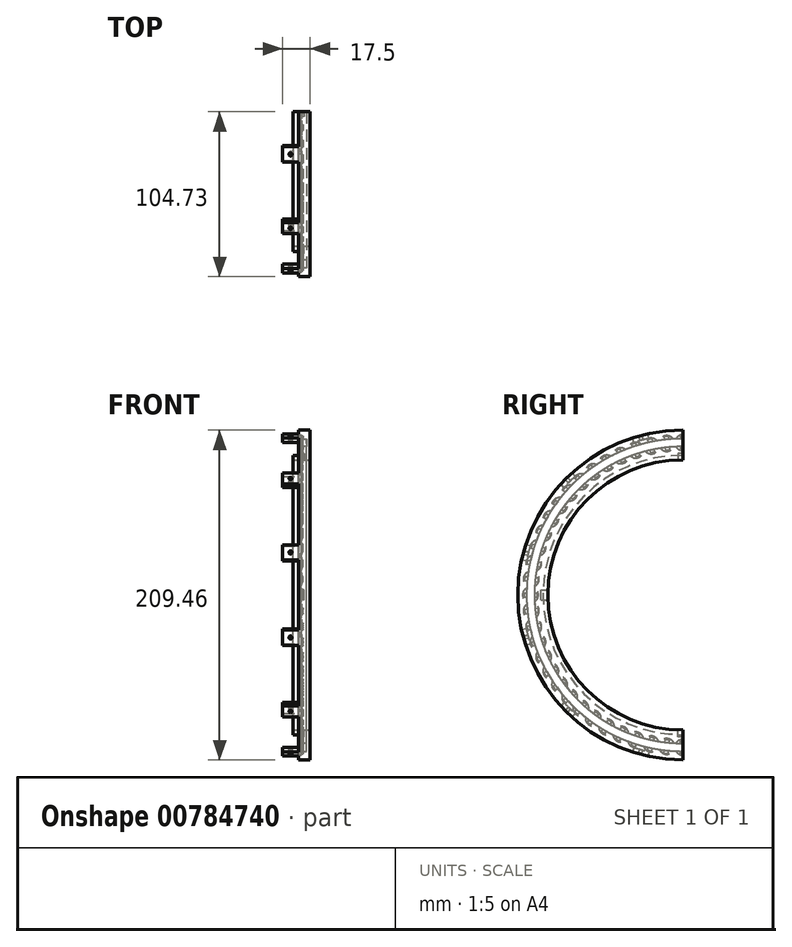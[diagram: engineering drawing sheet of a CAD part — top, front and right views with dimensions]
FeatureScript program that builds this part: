
annotation { "Feature Type Name" : "Feature", "Feature Type Description" : "" }
export const myFeature = defineFeature(function(context is Context, id is Id, definition is map)
    precondition{}
    {
        {
            var Q0;
            Q0=qCreatedBy(makeId("Front.planeOp"),FACE);
            var sketch = newSketch(context, id + "F0", { "sketchPlane" : qUnion([Q0])});
            skLineSegment(sketch, "E0.bottom", {"start": v(-125, 105) * mm, "end": v(125, 105) * mm, "construction": true});
            skLineSegment(sketch, "E0.top", {"start": v(-125, -105) * mm, "end": v(125, -105) * mm, "construction": true});
            skLineSegment(sketch, "E0.left", {"start": v(-125, 105) * mm, "end": v(-125, -105) * mm, "construction": true});
            skLineSegment(sketch, "E0.right", {"start": v(125, 105) * mm, "end": v(125, -105) * mm, "construction": true});
            skLineSegment(sketch, "E1", {"start": v(-16.75, 85.73) * mm, "end": v(-16.75, 88.73) * mm});
            skLineSegment(sketch, "E2", {"start": v(-16.75, 88.73) * mm, "end": v(-13.25, 88.73) * mm});
            skLineSegment(sketch, "E3", {"start": v(-16.75, 85.73) * mm, "end": v(-5.75, 85.73) * mm});
            skLineSegment(sketch, "E4", {"start": v(-5.75, 85.73) * mm, "end": v(-5.75, 104.73) * mm});
            skLineSegment(sketch, "E5", {"start": v(-13.25, 104.73) * mm, "end": v(-13.25, 99.23) * mm});
            skLineSegment(sketch, "E6", {"start": v(-13.25, 99.23) * mm, "end": v(-8.25, 99.23) * mm});
            skLineSegment(sketch, "E7", {"start": v(-8.25, 99.23) * mm, "end": v(-8.25, 94.23) * mm});
            skLineSegment(sketch, "E8", {"start": v(-8.25, 94.23) * mm, "end": v(-13.25, 94.23) * mm});
            skLineSegment(sketch, "E9.trimOffspring", {"start": v(-13.25, 94.23) * mm, "end": v(-13.25, 88.73) * mm});
            skLineSegment(sketch, "E10", {"start": v(-74.95, 0) * mm, "end": v(74.95, 0) * mm});
            skLineSegment(sketch, "E11", {"start": v(-13.25, 104.73) * mm, "end": v(-8.75, 104.73) * mm});
            skLineSegment(sketch, "E12.trimOffspring", {"start": v(-7.75, 104.73) * mm, "end": v(-5.75, 104.73) * mm});
            skLineSegment(sketch, "E13", {"start": v(-7.75, 104.73) * mm, "end": v(-8.75, 104.73) * mm});
            skSolve(sketch);
        }
        {
            var Q0;
            Q0=qSketchRegion(id+"F0",true);
            var Q1;
            Q1=sQuery(id+"F0.wireOp",EDGE,"E10");
            revolve(context, id + "F1", {"surfaceOperationType" : NewSurfaceOperationType.NEW, "entities" : qUnion([Q0]), "axis" : qUnion([Q1]), "revolveType" : RevolveType.ONE_DIRECTION, "angle" : 180 * degree});
        }
        {
            var Q0;
            Q0=qCreatedBy(makeId("Top.planeOp"),FACE);
            cPlane(context, id + "F2", {"entities" : qUnion([Q0]), "cplaneType" : CPlaneType.OFFSET, "offset" : 80 * mm, "oppositeDirection" : true, "width" : 150 * mm, "height" : 150 * mm});
        }
        {
            var Q0;
            Q0=qCreatedBy(id+"F2.planeOp",FACE);
            var sketch = newSketch(context, id + "F3", { "sketchPlane" : qUnion([Q0])});
            skLineSegment(sketch, "E14.top", {"start": v(-9.65, -3.1) * mm, "end": v(-12.85, -3.1) * mm});
            skLineSegment(sketch, "E14.left", {"start": v(-9.65, 0) * mm, "end": v(-9.65, -3.1) * mm});
            skLineSegment(sketch, "E14.right", {"start": v(-12.85, 0) * mm, "end": v(-12.85, -3.1) * mm});
            skLineSegment(sketch, "E15.top", {"start": v(-9.65, 1.57) * mm, "end": v(-12.85, 1.57) * mm});
            skLineSegment(sketch, "E15.left", {"start": v(-9.65, 0) * mm, "end": v(-9.65, 1.57) * mm});
            skLineSegment(sketch, "E15.right", {"start": v(-12.85, 0) * mm, "end": v(-12.85, 1.57) * mm});
            skSolve(sketch);
        }
        {
            var Q0;
            Q0=qSketchRegion(id+"F3",true);
            var Q1;
            Q1=makeQuery(id+"F1.opRevolve","SWEPT_FACE",FACE,{"disambiguationData":[OSD([sQuery(id+"F0.wireOp",EDGE,"E2")])]});
            extrude(context, id + "F4", {"entities" : qUnion([Q0]), "operationType" : NewBodyOperationType.REMOVE, "oppositeDirection" : true, "depth" : 10 * mm, "endBoundEntityFace" : qUnion([Q1]), "offsetDistance" : 25 * mm});
        }
        {
            var Q0;
            Q0=qCreatedBy(makeId("Front.planeOp"),FACE);
            cPlane(context, id + "F5", {"entities" : qUnion([Q0]), "cplaneType" : CPlaneType.OFFSET, "offset" : 80 * mm, "width" : 150 * mm, "height" : 150 * mm});
        }
        {
            var Q0;
            Q0=qCreatedBy(makeId("Top.planeOp"),FACE);
            cPlane(context, id + "F6", {"entities" : qUnion([Q0]), "cplaneType" : CPlaneType.OFFSET, "offset" : 80 * mm, "width" : 150 * mm, "height" : 150 * mm});
        }
        {
            var Q0;
            Q0=qCreatedBy(id+"F5.planeOp",FACE);
            var sketch = newSketch(context, id + "F7", { "sketchPlane" : qUnion([Q0])});
            skLineSegment(sketch, "E16.bottom", {"start": v(-9.65, -3.1) * mm, "end": v(-12.85, -3.1) * mm});
            skLineSegment(sketch, "E16.top", {"start": v(-9.65, 3.1) * mm, "end": v(-12.85, 3.1) * mm});
            skLineSegment(sketch, "E16.left", {"start": v(-9.65, -3.1) * mm, "end": v(-9.65, 3.1) * mm});
            skLineSegment(sketch, "E16.right", {"start": v(-12.85, -3.1) * mm, "end": v(-12.85, 3.1) * mm});
            skSolve(sketch);
        }
        {
            var Q0;
            Q0=qSketchRegion(id+"F7",true);
            var Q1;
            Q1=makeQuery(id+"F1.opRevolve","SWEPT_FACE",FACE,{"disambiguationData":[OSD([sQuery(id+"F0.wireOp",EDGE,"E2")])]});
            extrude(context, id + "F8", {"entities" : qUnion([Q0]), "operationType" : NewBodyOperationType.REMOVE, "depth" : 10 * mm, "endBoundEntityFace" : qUnion([Q1]), "offsetDistance" : 25 * mm});
        }
        {
            var Q0;
            Q0=qCreatedBy(id+"F6.planeOp",FACE);
            var sketch = newSketch(context, id + "F9", { "sketchPlane" : qUnion([Q0])});
            skLineSegment(sketch, "E17.bottom", {"start": v(-9.65, 0) * mm, "end": v(-12.85, 0) * mm});
            skLineSegment(sketch, "E17.top", {"start": v(-9.65, -3.1) * mm, "end": v(-12.85, -3.1) * mm});
            skLineSegment(sketch, "E17.left", {"start": v(-9.65, 0) * mm, "end": v(-9.65, -3.1) * mm});
            skLineSegment(sketch, "E17.right", {"start": v(-12.85, 0) * mm, "end": v(-12.85, -3.1) * mm});
            skSolve(sketch);
        }
        {
            var Q0;
            Q0=qSketchRegion(id+"F9",true);
            var Q1;
            Q1=makeQuery(id+"F1.opRevolve","SWEPT_FACE",FACE,{"disambiguationData":[OSD([sQuery(id+"F0.wireOp",EDGE,"E2")])]});
            extrude(context, id + "F10", {"entities" : qUnion([Q0]), "operationType" : NewBodyOperationType.REMOVE, "depth" : 10 * mm, "endBoundEntityFace" : qUnion([Q1]), "offsetDistance" : 25 * mm});
        }
        {
            var Q0;
            Q0=makeQuery(id+"F1.opRevolve","SWEPT_FACE",FACE,{"disambiguationData":[OSD([sQuery(id+"F0.wireOp",EDGE,"E7")])]});
            var sketch = newSketch(context, id + "F11", { "sketchPlane" : qUnion([Q0])});
            skCircle(sketch, "E18", {"center": v(0, 96.73) * mm, "radius": 5 * mm});
            skCircle(sketch, "E19.1.0", {"center": v(-10.11, 96.2) * mm, "radius": 5 * mm});
            skCircle(sketch, "E19.2.0", {"center": v(-20.11, 94.62) * mm, "radius": 5 * mm});
            skCircle(sketch, "E19.3.0", {"center": v(-29.9, 92) * mm, "radius": 5 * mm});
            skCircle(sketch, "E19.4.0", {"center": v(-39.34, 88.37) * mm, "radius": 5 * mm});
            skCircle(sketch, "E19.5.0", {"center": v(-48.36, 83.77) * mm, "radius": 5 * mm});
            skCircle(sketch, "E19.6.0", {"center": v(-56.86, 78.26) * mm, "radius": 5 * mm});
            skCircle(sketch, "E19.7.0", {"center": v(-64.73, 71.88) * mm, "radius": 5 * mm});
            skCircle(sketch, "E19.8.0", {"center": v(-71.88, 64.73) * mm, "radius": 5 * mm});
            skCircle(sketch, "E19.9.0", {"center": v(-78.26, 56.86) * mm, "radius": 5 * mm});
            skCircle(sketch, "E19.10.0", {"center": v(-83.77, 48.36) * mm, "radius": 5 * mm});
            skCircle(sketch, "E19.11.0", {"center": v(-88.37, 39.34) * mm, "radius": 5 * mm});
            skCircle(sketch, "E19.12.0", {"center": v(-92, 29.9) * mm, "radius": 5 * mm});
            skCircle(sketch, "E19.13.0", {"center": v(-94.62, 20.11) * mm, "radius": 5 * mm});
            skCircle(sketch, "E19.14.0", {"center": v(-96.2, 10.11) * mm, "radius": 5 * mm});
            skCircle(sketch, "E19.15.0", {"center": v(-96.73, 0) * mm, "radius": 5 * mm});
            skCircle(sketch, "E19.16.0", {"center": v(-96.2, -10.11) * mm, "radius": 5 * mm});
            skCircle(sketch, "E19.17.0", {"center": v(-94.62, -20.11) * mm, "radius": 5 * mm});
            skCircle(sketch, "E19.18.0", {"center": v(-92, -29.9) * mm, "radius": 5 * mm});
            skCircle(sketch, "E19.19.0", {"center": v(-88.37, -39.34) * mm, "radius": 5 * mm});
            skCircle(sketch, "E19.20.0", {"center": v(-83.77, -48.36) * mm, "radius": 5 * mm});
            skCircle(sketch, "E19.21.0", {"center": v(-78.26, -56.86) * mm, "radius": 5 * mm});
            skCircle(sketch, "E19.22.0", {"center": v(-71.88, -64.73) * mm, "radius": 5 * mm});
            skCircle(sketch, "E19.23.0", {"center": v(-64.73, -71.88) * mm, "radius": 5 * mm});
            skCircle(sketch, "E19.24.0", {"center": v(-56.86, -78.26) * mm, "radius": 5 * mm});
            skCircle(sketch, "E19.25.0", {"center": v(-48.36, -83.77) * mm, "radius": 5 * mm});
            skCircle(sketch, "E19.26.0", {"center": v(-39.34, -88.37) * mm, "radius": 5 * mm});
            skCircle(sketch, "E19.27.0", {"center": v(-29.9, -92) * mm, "radius": 5 * mm});
            skCircle(sketch, "E19.28.0", {"center": v(-20.11, -94.62) * mm, "radius": 5 * mm});
            skCircle(sketch, "E19.29.0", {"center": v(-10.11, -96.2) * mm, "radius": 5 * mm});
            skCircle(sketch, "E19.30.0", {"center": v(0, -96.73) * mm, "radius": 5 * mm});
            skCircle(sketch, "E19.31.0", {"center": v(10.11, -96.2) * mm, "radius": 5 * mm});
            skCircle(sketch, "E19.32.0", {"center": v(20.11, -94.62) * mm, "radius": 5 * mm});
            skCircle(sketch, "E19.33.0", {"center": v(29.9, -92) * mm, "radius": 5 * mm});
            skCircle(sketch, "E19.34.0", {"center": v(39.34, -88.37) * mm, "radius": 5 * mm});
            skCircle(sketch, "E19.35.0", {"center": v(48.36, -83.77) * mm, "radius": 5 * mm});
            skCircle(sketch, "E19.36.0", {"center": v(56.86, -78.26) * mm, "radius": 5 * mm});
            skCircle(sketch, "E19.37.0", {"center": v(64.73, -71.88) * mm, "radius": 5 * mm});
            skCircle(sketch, "E19.38.0", {"center": v(71.88, -64.73) * mm, "radius": 5 * mm});
            skCircle(sketch, "E19.39.0", {"center": v(78.26, -56.86) * mm, "radius": 5 * mm});
            skCircle(sketch, "E19.40.0", {"center": v(83.77, -48.37) * mm, "radius": 5 * mm});
            skCircle(sketch, "E19.41.0", {"center": v(88.37, -39.34) * mm, "radius": 5 * mm});
            skCircle(sketch, "E19.42.0", {"center": v(92, -29.9) * mm, "radius": 5 * mm});
            skCircle(sketch, "E19.43.0", {"center": v(94.62, -20.11) * mm, "radius": 5 * mm});
            skCircle(sketch, "E19.44.0", {"center": v(96.2, -10.11) * mm, "radius": 5 * mm});
            skCircle(sketch, "E19.45.0", {"center": v(96.73, 0) * mm, "radius": 5 * mm});
            skCircle(sketch, "E19.46.0", {"center": v(96.2, 10.11) * mm, "radius": 5 * mm});
            skCircle(sketch, "E19.47.0", {"center": v(94.62, 20.11) * mm, "radius": 5 * mm});
            skCircle(sketch, "E19.48.0", {"center": v(92, 29.9) * mm, "radius": 5 * mm});
            skCircle(sketch, "E19.49.0", {"center": v(88.37, 39.34) * mm, "radius": 5 * mm});
            skCircle(sketch, "E19.50.0", {"center": v(83.77, 48.36) * mm, "radius": 5 * mm});
            skCircle(sketch, "E19.51.0", {"center": v(78.26, 56.86) * mm, "radius": 5 * mm});
            skCircle(sketch, "E19.52.0", {"center": v(71.88, 64.73) * mm, "radius": 5 * mm});
            skCircle(sketch, "E19.53.0", {"center": v(64.73, 71.88) * mm, "radius": 5 * mm});
            skCircle(sketch, "E19.54.0", {"center": v(56.86, 78.26) * mm, "radius": 5 * mm});
            skCircle(sketch, "E19.55.0", {"center": v(48.36, 83.77) * mm, "radius": 5 * mm});
            skCircle(sketch, "E19.56.0", {"center": v(39.34, 88.37) * mm, "radius": 5 * mm});
            skCircle(sketch, "E19.57.0", {"center": v(29.9, 92) * mm, "radius": 5 * mm});
            skCircle(sketch, "E19.58.0", {"center": v(20.11, 94.62) * mm, "radius": 5 * mm});
            skCircle(sketch, "E19.59.0", {"center": v(10.11, 96.2) * mm, "radius": 5 * mm});
            skPoint(sketch, "E19.center", {"position": v(0, 0) * mm});
            skSolve(sketch);
        }
        {
            var Q0;
            Q0=qSketchRegion(id+"F11",true);
            extrude(context, id + "F12", {"entities" : qUnion([Q0]), "operationType" : NewBodyOperationType.REMOVE, "depth" : 25 * mm, "offsetDistance" : 25 * mm, "hasSecondDirection" : true, "secondDirectionOppositeDirection" : false, "secondDirectionDepth" : 3 * mm});
        }
        {
            var Q0;
            Q0=makeQuery(id+"F1.opRevolve","SWEPT_FACE",FACE,{"disambiguationData":[OSD([sQuery(id+"F0.wireOp",EDGE,"E7")])]});
            var sketch = newSketch(context, id + "F13", { "sketchPlane" : qUnion([Q0])});
            skLineSegment(sketch, "E20.bottom", {"start": v(1.36, 92.48) * mm, "end": v(0, 92.48) * mm});
            skLineSegment(sketch, "E20.top", {"start": v(1.36, 100.98) * mm, "end": v(0, 100.98) * mm});
            skLineSegment(sketch, "E20.left", {"start": v(1.36, 92.48) * mm, "end": v(1.36, 100.98) * mm});
            skLineSegment(sketch, "E21", {"start": v(1.96, 96.73) * mm, "end": v(-1.46, 96.73) * mm, "construction": true});
            skLineSegment(sketch, "E22.MirrorCS", {"start": v(-1.36, 92.48) * mm, "end": v(0, 92.48) * mm});
            skLineSegment(sketch, "E23.MirrorCS", {"start": v(-1.36, 92.48) * mm, "end": v(-1.36, 100.98) * mm});
            skLineSegment(sketch, "E24.MirrorCS", {"start": v(-1.36, 100.98) * mm, "end": v(0, 100.98) * mm});
            skLineSegment(sketch, "E25", {"start": v(0, 92.48) * mm, "end": v(0, 100.98) * mm, "construction": true});
            skLineSegment(sketch, "E26.1.0", {"start": v(-8.32, 92.12) * mm, "end": v(-9.67, 91.97) * mm});
            skLineSegment(sketch, "E26.1.1", {"start": v(-9.2, 100.57) * mm, "end": v(-10.56, 100.43) * mm});
            skLineSegment(sketch, "E26.1.2", {"start": v(-8.32, 92.12) * mm, "end": v(-9.2, 100.57) * mm});
            skLineSegment(sketch, "E26.1.3", {"start": v(-8.16, 96.4) * mm, "end": v(-11.56, 96.05) * mm, "construction": true});
            skLineSegment(sketch, "E26.1.4", {"start": v(-11.02, 91.83) * mm, "end": v(-9.67, 91.97) * mm});
            skLineSegment(sketch, "E26.1.5", {"start": v(-11.02, 91.83) * mm, "end": v(-11.9, 100.28) * mm});
            skLineSegment(sketch, "E26.1.6", {"start": v(-11.9, 100.28) * mm, "end": v(-10.56, 100.43) * mm});
            skLineSegment(sketch, "E26.1.7", {"start": v(-9.67, 91.97) * mm, "end": v(-10.56, 100.43) * mm, "construction": true});
            skLineSegment(sketch, "E26.2.0", {"start": v(-17.9, 90.74) * mm, "end": v(-19.23, 90.46) * mm});
            skLineSegment(sketch, "E26.2.1", {"start": v(-19.67, 99.06) * mm, "end": v(-21, 98.77) * mm});
            skLineSegment(sketch, "E26.2.2", {"start": v(-17.9, 90.74) * mm, "end": v(-19.67, 99.06) * mm});
            skLineSegment(sketch, "E26.2.3", {"start": v(-18.2, 95.02) * mm, "end": v(-21.54, 94.31) * mm, "construction": true});
            skLineSegment(sketch, "E26.2.4", {"start": v(-20.56, 90.18) * mm, "end": v(-19.23, 90.46) * mm});
            skLineSegment(sketch, "E26.2.5", {"start": v(-20.56, 90.18) * mm, "end": v(-22.32, 98.5) * mm});
            skLineSegment(sketch, "E26.2.6", {"start": v(-22.32, 98.5) * mm, "end": v(-21, 98.77) * mm});
            skLineSegment(sketch, "E26.2.7", {"start": v(-19.23, 90.46) * mm, "end": v(-21, 98.77) * mm, "construction": true});
            skLineSegment(sketch, "E26.3.0", {"start": v(-27.29, 88.37) * mm, "end": v(-28.58, 87.95) * mm});
            skLineSegment(sketch, "E26.3.1", {"start": v(-29.91, 96.46) * mm, "end": v(-31.2, 96.04) * mm});
            skLineSegment(sketch, "E26.3.2", {"start": v(-27.29, 88.37) * mm, "end": v(-29.91, 96.46) * mm});
            skLineSegment(sketch, "E26.3.3", {"start": v(-28.02, 92.6) * mm, "end": v(-31.28, 91.54) * mm, "construction": true});
            skLineSegment(sketch, "E26.3.4", {"start": v(-29.87, 87.53) * mm, "end": v(-28.58, 87.95) * mm});
            skLineSegment(sketch, "E26.3.5", {"start": v(-29.87, 87.53) * mm, "end": v(-32.5, 95.62) * mm});
            skLineSegment(sketch, "E26.3.6", {"start": v(-32.5, 95.62) * mm, "end": v(-31.2, 96.04) * mm});
            skLineSegment(sketch, "E26.3.7", {"start": v(-28.58, 87.95) * mm, "end": v(-31.2, 96.04) * mm, "construction": true});
            skLineSegment(sketch, "E26.4.0", {"start": v(-36.37, 85.04) * mm, "end": v(-37.62, 84.48) * mm});
            skLineSegment(sketch, "E26.4.1", {"start": v(-39.83, 92.8) * mm, "end": v(-41.07, 92.25) * mm});
            skLineSegment(sketch, "E26.4.2", {"start": v(-36.37, 85.04) * mm, "end": v(-39.83, 92.8) * mm});
            skLineSegment(sketch, "E26.4.3", {"start": v(-37.55, 89.17) * mm, "end": v(-40.68, 87.77) * mm, "construction": true});
            skLineSegment(sketch, "E26.4.4", {"start": v(-38.86, 83.93) * mm, "end": v(-37.62, 84.48) * mm});
            skLineSegment(sketch, "E26.4.5", {"start": v(-38.86, 83.93) * mm, "end": v(-42.31, 91.7) * mm});
            skLineSegment(sketch, "E26.4.6", {"start": v(-42.31, 91.7) * mm, "end": v(-41.07, 92.25) * mm});
            skLineSegment(sketch, "E26.4.7", {"start": v(-37.62, 84.48) * mm, "end": v(-41.07, 92.25) * mm, "construction": true});
            skLineSegment(sketch, "E26.5.0", {"start": v(-45.06, 80.77) * mm, "end": v(-46.24, 80.1) * mm});
            skLineSegment(sketch, "E26.5.1", {"start": v(-49.31, 88.13) * mm, "end": v(-50.49, 87.45) * mm});
            skLineSegment(sketch, "E26.5.2", {"start": v(-45.06, 80.77) * mm, "end": v(-49.31, 88.13) * mm});
            skLineSegment(sketch, "E26.5.3", {"start": v(-46.67, 84.75) * mm, "end": v(-49.63, 83.04) * mm, "construction": true});
            skLineSegment(sketch, "E26.5.4", {"start": v(-47.42, 79.41) * mm, "end": v(-46.24, 80.1) * mm});
            skLineSegment(sketch, "E26.5.5", {"start": v(-47.42, 79.41) * mm, "end": v(-51.67, 86.77) * mm});
            skLineSegment(sketch, "E26.5.6", {"start": v(-51.67, 86.77) * mm, "end": v(-50.49, 87.45) * mm});
            skLineSegment(sketch, "E26.5.7", {"start": v(-46.24, 80.1) * mm, "end": v(-50.49, 87.45) * mm, "construction": true});
            skLineSegment(sketch, "E26.6.0", {"start": v(-53.26, 75.62) * mm, "end": v(-54.36, 74.82) * mm});
            skLineSegment(sketch, "E26.6.1", {"start": v(-58.26, 82.5) * mm, "end": v(-59.35, 81.7) * mm});
            skLineSegment(sketch, "E26.6.2", {"start": v(-53.26, 75.62) * mm, "end": v(-58.26, 82.5) * mm});
            skLineSegment(sketch, "E26.6.3", {"start": v(-55.27, 79.4) * mm, "end": v(-58.04, 77.4) * mm, "construction": true});
            skLineSegment(sketch, "E26.6.4", {"start": v(-55.46, 74.02) * mm, "end": v(-54.36, 74.82) * mm});
            skLineSegment(sketch, "E26.6.5", {"start": v(-55.46, 74.02) * mm, "end": v(-60.45, 80.9) * mm});
            skLineSegment(sketch, "E26.6.6", {"start": v(-60.45, 80.9) * mm, "end": v(-59.35, 81.7) * mm});
            skLineSegment(sketch, "E26.6.7", {"start": v(-54.36, 74.82) * mm, "end": v(-59.35, 81.7) * mm, "construction": true});
            skLineSegment(sketch, "E26.7.0", {"start": v(-60.87, 69.63) * mm, "end": v(-61.88, 68.73) * mm});
            skLineSegment(sketch, "E26.7.1", {"start": v(-66.56, 75.95) * mm, "end": v(-67.57, 75.04) * mm});
            skLineSegment(sketch, "E26.7.2", {"start": v(-60.87, 69.63) * mm, "end": v(-66.56, 75.95) * mm});
            skLineSegment(sketch, "E26.7.3", {"start": v(-63.27, 73.2) * mm, "end": v(-65.8, 70.9) * mm, "construction": true});
            skLineSegment(sketch, "E26.7.4", {"start": v(-62.9, 67.82) * mm, "end": v(-61.88, 68.73) * mm});
            skLineSegment(sketch, "E26.7.5", {"start": v(-62.9, 67.82) * mm, "end": v(-68.58, 74.13) * mm});
            skLineSegment(sketch, "E26.7.6", {"start": v(-68.58, 74.13) * mm, "end": v(-67.57, 75.04) * mm});
            skLineSegment(sketch, "E26.7.7", {"start": v(-61.88, 68.73) * mm, "end": v(-67.57, 75.04) * mm, "construction": true});
            skLineSegment(sketch, "E26.8.0", {"start": v(-67.82, 62.9) * mm, "end": v(-68.73, 61.88) * mm});
            skLineSegment(sketch, "E26.8.1", {"start": v(-74.13, 68.58) * mm, "end": v(-75.04, 67.57) * mm});
            skLineSegment(sketch, "E26.8.2", {"start": v(-67.82, 62.9) * mm, "end": v(-74.13, 68.58) * mm});
            skLineSegment(sketch, "E26.8.3", {"start": v(-70.57, 66.18) * mm, "end": v(-72.86, 63.64) * mm, "construction": true});
            skLineSegment(sketch, "E26.8.4", {"start": v(-69.63, 60.87) * mm, "end": v(-68.73, 61.88) * mm});
            skLineSegment(sketch, "E26.8.5", {"start": v(-69.63, 60.87) * mm, "end": v(-75.95, 66.56) * mm});
            skLineSegment(sketch, "E26.8.6", {"start": v(-75.95, 66.56) * mm, "end": v(-75.04, 67.57) * mm});
            skLineSegment(sketch, "E26.8.7", {"start": v(-68.73, 61.88) * mm, "end": v(-75.04, 67.57) * mm, "construction": true});
            skLineSegment(sketch, "E26.9.0", {"start": v(-74.02, 55.46) * mm, "end": v(-74.82, 54.36) * mm});
            skLineSegment(sketch, "E26.9.1", {"start": v(-80.9, 60.45) * mm, "end": v(-81.7, 59.35) * mm});
            skLineSegment(sketch, "E26.9.2", {"start": v(-74.02, 55.46) * mm, "end": v(-80.9, 60.45) * mm});
            skLineSegment(sketch, "E26.9.3", {"start": v(-77.1, 58.44) * mm, "end": v(-79.11, 55.68) * mm, "construction": true});
            skLineSegment(sketch, "E26.9.4", {"start": v(-75.62, 53.26) * mm, "end": v(-74.82, 54.36) * mm});
            skLineSegment(sketch, "E26.9.5", {"start": v(-75.62, 53.26) * mm, "end": v(-82.5, 58.26) * mm});
            skLineSegment(sketch, "E26.9.6", {"start": v(-82.5, 58.26) * mm, "end": v(-81.7, 59.35) * mm});
            skLineSegment(sketch, "E26.9.7", {"start": v(-74.82, 54.36) * mm, "end": v(-81.7, 59.35) * mm, "construction": true});
            skLineSegment(sketch, "E26.10.0", {"start": v(-79.41, 47.42) * mm, "end": v(-80.1, 46.24) * mm});
            skLineSegment(sketch, "E26.10.1", {"start": v(-86.77, 51.67) * mm, "end": v(-87.45, 50.49) * mm});
            skLineSegment(sketch, "E26.10.2", {"start": v(-79.41, 47.42) * mm, "end": v(-86.77, 51.67) * mm});
            skLineSegment(sketch, "E26.10.3", {"start": v(-82.79, 50.06) * mm, "end": v(-84.5, 47.1) * mm, "construction": true});
            skLineSegment(sketch, "E26.10.4", {"start": v(-80.77, 45.06) * mm, "end": v(-80.1, 46.24) * mm});
            skLineSegment(sketch, "E26.10.5", {"start": v(-80.77, 45.06) * mm, "end": v(-88.13, 49.31) * mm});
            skLineSegment(sketch, "E26.10.6", {"start": v(-88.13, 49.31) * mm, "end": v(-87.45, 50.49) * mm});
            skLineSegment(sketch, "E26.10.7", {"start": v(-80.1, 46.24) * mm, "end": v(-87.45, 50.49) * mm, "construction": true});
            skLineSegment(sketch, "E26.11.0", {"start": v(-83.93, 38.86) * mm, "end": v(-84.48, 37.62) * mm});
            skLineSegment(sketch, "E26.11.1", {"start": v(-91.7, 42.31) * mm, "end": v(-92.25, 41.07) * mm});
            skLineSegment(sketch, "E26.11.2", {"start": v(-83.93, 38.86) * mm, "end": v(-91.7, 42.31) * mm});
            skLineSegment(sketch, "E26.11.3", {"start": v(-87.57, 41.14) * mm, "end": v(-88.96, 38) * mm, "construction": true});
            skLineSegment(sketch, "E26.11.4", {"start": v(-85.04, 36.37) * mm, "end": v(-84.48, 37.62) * mm});
            skLineSegment(sketch, "E26.11.5", {"start": v(-85.04, 36.37) * mm, "end": v(-92.8, 39.83) * mm});
            skLineSegment(sketch, "E26.11.6", {"start": v(-92.8, 39.83) * mm, "end": v(-92.25, 41.07) * mm});
            skLineSegment(sketch, "E26.11.7", {"start": v(-84.48, 37.62) * mm, "end": v(-92.25, 41.07) * mm, "construction": true});
            skLineSegment(sketch, "E26.12.0", {"start": v(-87.53, 29.87) * mm, "end": v(-87.95, 28.58) * mm});
            skLineSegment(sketch, "E26.12.1", {"start": v(-95.62, 32.5) * mm, "end": v(-96.04, 31.2) * mm});
            skLineSegment(sketch, "E26.12.2", {"start": v(-87.53, 29.87) * mm, "end": v(-95.62, 32.5) * mm});
            skLineSegment(sketch, "E26.12.3", {"start": v(-91.39, 31.76) * mm, "end": v(-92.45, 28.5) * mm, "construction": true});
            skLineSegment(sketch, "E26.12.4", {"start": v(-88.37, 27.29) * mm, "end": v(-87.95, 28.58) * mm});
            skLineSegment(sketch, "E26.12.5", {"start": v(-88.37, 27.29) * mm, "end": v(-96.46, 29.91) * mm});
            skLineSegment(sketch, "E26.12.6", {"start": v(-96.46, 29.91) * mm, "end": v(-96.04, 31.2) * mm});
            skLineSegment(sketch, "E26.12.7", {"start": v(-87.95, 28.58) * mm, "end": v(-96.04, 31.2) * mm, "construction": true});
            skLineSegment(sketch, "E26.13.0", {"start": v(-90.18, 20.56) * mm, "end": v(-90.46, 19.23) * mm});
            skLineSegment(sketch, "E26.13.1", {"start": v(-98.5, 22.32) * mm, "end": v(-98.77, 21) * mm});
            skLineSegment(sketch, "E26.13.2", {"start": v(-90.18, 20.56) * mm, "end": v(-98.5, 22.32) * mm});
            skLineSegment(sketch, "E26.13.3", {"start": v(-94.2, 22.03) * mm, "end": v(-94.92, 18.68) * mm, "construction": true});
            skLineSegment(sketch, "E26.13.4", {"start": v(-90.74, 17.9) * mm, "end": v(-90.46, 19.23) * mm});
            skLineSegment(sketch, "E26.13.5", {"start": v(-90.74, 17.9) * mm, "end": v(-99.06, 19.67) * mm});
            skLineSegment(sketch, "E26.13.6", {"start": v(-99.06, 19.67) * mm, "end": v(-98.77, 21) * mm});
            skLineSegment(sketch, "E26.13.7", {"start": v(-90.46, 19.23) * mm, "end": v(-98.77, 21) * mm, "construction": true});
            skLineSegment(sketch, "E26.14.0", {"start": v(-91.83, 11.02) * mm, "end": v(-91.97, 9.67) * mm});
            skLineSegment(sketch, "E26.14.1", {"start": v(-100.28, 11.9) * mm, "end": v(-100.43, 10.56) * mm});
            skLineSegment(sketch, "E26.14.2", {"start": v(-91.83, 11.02) * mm, "end": v(-100.28, 11.9) * mm});
            skLineSegment(sketch, "E26.14.3", {"start": v(-96, 12.06) * mm, "end": v(-96.35, 8.66) * mm, "construction": true});
            skLineSegment(sketch, "E26.14.4", {"start": v(-92.12, 8.32) * mm, "end": v(-91.97, 9.67) * mm});
            skLineSegment(sketch, "E26.14.5", {"start": v(-92.12, 8.32) * mm, "end": v(-100.57, 9.2) * mm});
            skLineSegment(sketch, "E26.14.6", {"start": v(-100.57, 9.2) * mm, "end": v(-100.43, 10.56) * mm});
            skLineSegment(sketch, "E26.14.7", {"start": v(-91.97, 9.67) * mm, "end": v(-100.43, 10.56) * mm, "construction": true});
            skLineSegment(sketch, "E26.15.0", {"start": v(-92.48, 1.36) * mm, "end": v(-92.48, 0) * mm});
            skLineSegment(sketch, "E26.15.1", {"start": v(-100.98, 1.36) * mm, "end": v(-100.98, 0) * mm});
            skLineSegment(sketch, "E26.15.2", {"start": v(-92.48, 1.36) * mm, "end": v(-100.98, 1.36) * mm});
            skLineSegment(sketch, "E26.15.3", {"start": v(-96.73, 1.96) * mm, "end": v(-96.73, -1.46) * mm, "construction": true});
            skLineSegment(sketch, "E26.15.4", {"start": v(-92.48, -1.36) * mm, "end": v(-92.48, 0) * mm});
            skLineSegment(sketch, "E26.15.5", {"start": v(-92.48, -1.36) * mm, "end": v(-100.98, -1.36) * mm});
            skLineSegment(sketch, "E26.15.6", {"start": v(-100.98, -1.36) * mm, "end": v(-100.98, 0) * mm});
            skLineSegment(sketch, "E26.15.7", {"start": v(-92.48, 0) * mm, "end": v(-100.98, 0) * mm, "construction": true});
            skLineSegment(sketch, "E26.16.0", {"start": v(-92.12, -8.32) * mm, "end": v(-91.97, -9.67) * mm});
            skLineSegment(sketch, "E26.16.1", {"start": v(-100.57, -9.2) * mm, "end": v(-100.43, -10.56) * mm});
            skLineSegment(sketch, "E26.16.2", {"start": v(-92.12, -8.32) * mm, "end": v(-100.57, -9.2) * mm});
            skLineSegment(sketch, "E26.16.3", {"start": v(-96.4, -8.16) * mm, "end": v(-96.05, -11.56) * mm, "construction": true});
            skLineSegment(sketch, "E26.16.4", {"start": v(-91.83, -11.02) * mm, "end": v(-91.97, -9.67) * mm});
            skLineSegment(sketch, "E26.16.5", {"start": v(-91.83, -11.02) * mm, "end": v(-100.28, -11.9) * mm});
            skLineSegment(sketch, "E26.16.6", {"start": v(-100.28, -11.9) * mm, "end": v(-100.43, -10.56) * mm});
            skLineSegment(sketch, "E26.16.7", {"start": v(-91.97, -9.67) * mm, "end": v(-100.43, -10.56) * mm, "construction": true});
            skLineSegment(sketch, "E26.17.0", {"start": v(-90.74, -17.9) * mm, "end": v(-90.46, -19.23) * mm});
            skLineSegment(sketch, "E26.17.1", {"start": v(-99.06, -19.67) * mm, "end": v(-98.77, -21) * mm});
            skLineSegment(sketch, "E26.17.2", {"start": v(-90.74, -17.9) * mm, "end": v(-99.06, -19.67) * mm});
            skLineSegment(sketch, "E26.17.3", {"start": v(-95.02, -18.2) * mm, "end": v(-94.31, -21.54) * mm, "construction": true});
            skLineSegment(sketch, "E26.17.4", {"start": v(-90.18, -20.56) * mm, "end": v(-90.46, -19.23) * mm});
            skLineSegment(sketch, "E26.17.5", {"start": v(-90.18, -20.56) * mm, "end": v(-98.5, -22.32) * mm});
            skLineSegment(sketch, "E26.17.6", {"start": v(-98.5, -22.32) * mm, "end": v(-98.77, -21) * mm});
            skLineSegment(sketch, "E26.17.7", {"start": v(-90.46, -19.23) * mm, "end": v(-98.77, -21) * mm, "construction": true});
            skLineSegment(sketch, "E26.18.0", {"start": v(-88.37, -27.29) * mm, "end": v(-87.95, -28.58) * mm});
            skLineSegment(sketch, "E26.18.1", {"start": v(-96.46, -29.91) * mm, "end": v(-96.04, -31.2) * mm});
            skLineSegment(sketch, "E26.18.2", {"start": v(-88.37, -27.29) * mm, "end": v(-96.46, -29.91) * mm});
            skLineSegment(sketch, "E26.18.3", {"start": v(-92.6, -28.02) * mm, "end": v(-91.54, -31.28) * mm, "construction": true});
            skLineSegment(sketch, "E26.18.4", {"start": v(-87.53, -29.87) * mm, "end": v(-87.95, -28.58) * mm});
            skLineSegment(sketch, "E26.18.5", {"start": v(-87.53, -29.87) * mm, "end": v(-95.62, -32.5) * mm});
            skLineSegment(sketch, "E26.18.6", {"start": v(-95.62, -32.5) * mm, "end": v(-96.04, -31.2) * mm});
            skLineSegment(sketch, "E26.18.7", {"start": v(-87.95, -28.58) * mm, "end": v(-96.04, -31.2) * mm, "construction": true});
            skLineSegment(sketch, "E26.19.0", {"start": v(-85.04, -36.37) * mm, "end": v(-84.48, -37.62) * mm});
            skLineSegment(sketch, "E26.19.1", {"start": v(-92.8, -39.83) * mm, "end": v(-92.25, -41.07) * mm});
            skLineSegment(sketch, "E26.19.2", {"start": v(-85.04, -36.37) * mm, "end": v(-92.8, -39.83) * mm});
            skLineSegment(sketch, "E26.19.3", {"start": v(-89.17, -37.55) * mm, "end": v(-87.77, -40.68) * mm, "construction": true});
            skLineSegment(sketch, "E26.19.4", {"start": v(-83.93, -38.86) * mm, "end": v(-84.48, -37.62) * mm});
            skLineSegment(sketch, "E26.19.5", {"start": v(-83.93, -38.86) * mm, "end": v(-91.7, -42.31) * mm});
            skLineSegment(sketch, "E26.19.6", {"start": v(-91.7, -42.31) * mm, "end": v(-92.25, -41.07) * mm});
            skLineSegment(sketch, "E26.19.7", {"start": v(-84.48, -37.62) * mm, "end": v(-92.25, -41.07) * mm, "construction": true});
            skLineSegment(sketch, "E26.20.0", {"start": v(-80.77, -45.06) * mm, "end": v(-80.1, -46.24) * mm});
            skLineSegment(sketch, "E26.20.1", {"start": v(-88.13, -49.31) * mm, "end": v(-87.45, -50.49) * mm});
            skLineSegment(sketch, "E26.20.2", {"start": v(-80.77, -45.06) * mm, "end": v(-88.13, -49.31) * mm});
            skLineSegment(sketch, "E26.20.3", {"start": v(-84.75, -46.67) * mm, "end": v(-83.04, -49.63) * mm, "construction": true});
            skLineSegment(sketch, "E26.20.4", {"start": v(-79.41, -47.42) * mm, "end": v(-80.1, -46.24) * mm});
            skLineSegment(sketch, "E26.20.5", {"start": v(-79.41, -47.42) * mm, "end": v(-86.77, -51.67) * mm});
            skLineSegment(sketch, "E26.20.6", {"start": v(-86.77, -51.67) * mm, "end": v(-87.45, -50.49) * mm});
            skLineSegment(sketch, "E26.20.7", {"start": v(-80.1, -46.24) * mm, "end": v(-87.45, -50.49) * mm, "construction": true});
            skLineSegment(sketch, "E26.21.0", {"start": v(-75.62, -53.26) * mm, "end": v(-74.82, -54.36) * mm});
            skLineSegment(sketch, "E26.21.1", {"start": v(-82.5, -58.26) * mm, "end": v(-81.7, -59.35) * mm});
            skLineSegment(sketch, "E26.21.2", {"start": v(-75.62, -53.26) * mm, "end": v(-82.5, -58.26) * mm});
            skLineSegment(sketch, "E26.21.3", {"start": v(-79.4, -55.27) * mm, "end": v(-77.4, -58.04) * mm, "construction": true});
            skLineSegment(sketch, "E26.21.4", {"start": v(-74.02, -55.46) * mm, "end": v(-74.82, -54.36) * mm});
            skLineSegment(sketch, "E26.21.5", {"start": v(-74.02, -55.46) * mm, "end": v(-80.9, -60.45) * mm});
            skLineSegment(sketch, "E26.21.6", {"start": v(-80.9, -60.45) * mm, "end": v(-81.7, -59.35) * mm});
            skLineSegment(sketch, "E26.21.7", {"start": v(-74.82, -54.36) * mm, "end": v(-81.7, -59.35) * mm, "construction": true});
            skLineSegment(sketch, "E26.22.0", {"start": v(-69.63, -60.87) * mm, "end": v(-68.73, -61.88) * mm});
            skLineSegment(sketch, "E26.22.1", {"start": v(-75.95, -66.56) * mm, "end": v(-75.04, -67.57) * mm});
            skLineSegment(sketch, "E26.22.2", {"start": v(-69.63, -60.87) * mm, "end": v(-75.95, -66.56) * mm});
            skLineSegment(sketch, "E26.22.3", {"start": v(-73.2, -63.27) * mm, "end": v(-70.9, -65.8) * mm, "construction": true});
            skLineSegment(sketch, "E26.22.4", {"start": v(-67.82, -62.9) * mm, "end": v(-68.73, -61.88) * mm});
            skLineSegment(sketch, "E26.22.5", {"start": v(-67.82, -62.9) * mm, "end": v(-74.13, -68.58) * mm});
            skLineSegment(sketch, "E26.22.6", {"start": v(-74.13, -68.58) * mm, "end": v(-75.04, -67.57) * mm});
            skLineSegment(sketch, "E26.22.7", {"start": v(-68.73, -61.88) * mm, "end": v(-75.04, -67.57) * mm, "construction": true});
            skLineSegment(sketch, "E26.23.0", {"start": v(-62.9, -67.82) * mm, "end": v(-61.88, -68.73) * mm});
            skLineSegment(sketch, "E26.23.1", {"start": v(-68.58, -74.13) * mm, "end": v(-67.57, -75.04) * mm});
            skLineSegment(sketch, "E26.23.2", {"start": v(-62.9, -67.82) * mm, "end": v(-68.58, -74.13) * mm});
            skLineSegment(sketch, "E26.23.3", {"start": v(-66.18, -70.57) * mm, "end": v(-63.64, -72.86) * mm, "construction": true});
            skLineSegment(sketch, "E26.23.4", {"start": v(-60.87, -69.63) * mm, "end": v(-61.88, -68.73) * mm});
            skLineSegment(sketch, "E26.23.5", {"start": v(-60.87, -69.63) * mm, "end": v(-66.56, -75.95) * mm});
            skLineSegment(sketch, "E26.23.6", {"start": v(-66.56, -75.95) * mm, "end": v(-67.57, -75.04) * mm});
            skLineSegment(sketch, "E26.23.7", {"start": v(-61.88, -68.73) * mm, "end": v(-67.57, -75.04) * mm, "construction": true});
            skLineSegment(sketch, "E26.24.0", {"start": v(-55.46, -74.02) * mm, "end": v(-54.36, -74.82) * mm});
            skLineSegment(sketch, "E26.24.1", {"start": v(-60.45, -80.9) * mm, "end": v(-59.35, -81.7) * mm});
            skLineSegment(sketch, "E26.24.2", {"start": v(-55.46, -74.02) * mm, "end": v(-60.45, -80.9) * mm});
            skLineSegment(sketch, "E26.24.3", {"start": v(-58.44, -77.1) * mm, "end": v(-55.68, -79.11) * mm, "construction": true});
            skLineSegment(sketch, "E26.24.4", {"start": v(-53.26, -75.62) * mm, "end": v(-54.36, -74.82) * mm});
            skLineSegment(sketch, "E26.24.5", {"start": v(-53.26, -75.62) * mm, "end": v(-58.26, -82.5) * mm});
            skLineSegment(sketch, "E26.24.6", {"start": v(-58.26, -82.5) * mm, "end": v(-59.35, -81.7) * mm});
            skLineSegment(sketch, "E26.24.7", {"start": v(-54.36, -74.82) * mm, "end": v(-59.35, -81.7) * mm, "construction": true});
            skLineSegment(sketch, "E26.25.0", {"start": v(-47.42, -79.41) * mm, "end": v(-46.24, -80.1) * mm});
            skLineSegment(sketch, "E26.25.1", {"start": v(-51.67, -86.77) * mm, "end": v(-50.49, -87.45) * mm});
            skLineSegment(sketch, "E26.25.2", {"start": v(-47.42, -79.41) * mm, "end": v(-51.67, -86.77) * mm});
            skLineSegment(sketch, "E26.25.3", {"start": v(-50.06, -82.79) * mm, "end": v(-47.1, -84.5) * mm, "construction": true});
            skLineSegment(sketch, "E26.25.4", {"start": v(-45.06, -80.77) * mm, "end": v(-46.24, -80.1) * mm});
            skLineSegment(sketch, "E26.25.5", {"start": v(-45.06, -80.77) * mm, "end": v(-49.31, -88.13) * mm});
            skLineSegment(sketch, "E26.25.6", {"start": v(-49.31, -88.13) * mm, "end": v(-50.49, -87.45) * mm});
            skLineSegment(sketch, "E26.25.7", {"start": v(-46.24, -80.1) * mm, "end": v(-50.49, -87.45) * mm, "construction": true});
            skLineSegment(sketch, "E26.26.0", {"start": v(-38.86, -83.93) * mm, "end": v(-37.62, -84.48) * mm});
            skLineSegment(sketch, "E26.26.1", {"start": v(-42.31, -91.7) * mm, "end": v(-41.07, -92.25) * mm});
            skLineSegment(sketch, "E26.26.2", {"start": v(-38.86, -83.93) * mm, "end": v(-42.31, -91.7) * mm});
            skLineSegment(sketch, "E26.26.3", {"start": v(-41.14, -87.57) * mm, "end": v(-38, -88.96) * mm, "construction": true});
            skLineSegment(sketch, "E26.26.4", {"start": v(-36.37, -85.04) * mm, "end": v(-37.62, -84.48) * mm});
            skLineSegment(sketch, "E26.26.5", {"start": v(-36.37, -85.04) * mm, "end": v(-39.83, -92.8) * mm});
            skLineSegment(sketch, "E26.26.6", {"start": v(-39.83, -92.8) * mm, "end": v(-41.07, -92.25) * mm});
            skLineSegment(sketch, "E26.26.7", {"start": v(-37.62, -84.48) * mm, "end": v(-41.07, -92.25) * mm, "construction": true});
            skLineSegment(sketch, "E26.27.0", {"start": v(-29.87, -87.53) * mm, "end": v(-28.58, -87.95) * mm});
            skLineSegment(sketch, "E26.27.1", {"start": v(-32.5, -95.62) * mm, "end": v(-31.2, -96.04) * mm});
            skLineSegment(sketch, "E26.27.2", {"start": v(-29.87, -87.53) * mm, "end": v(-32.5, -95.62) * mm});
            skLineSegment(sketch, "E26.27.3", {"start": v(-31.76, -91.39) * mm, "end": v(-28.5, -92.45) * mm, "construction": true});
            skLineSegment(sketch, "E26.27.4", {"start": v(-27.29, -88.37) * mm, "end": v(-28.58, -87.95) * mm});
            skLineSegment(sketch, "E26.27.5", {"start": v(-27.29, -88.37) * mm, "end": v(-29.91, -96.46) * mm});
            skLineSegment(sketch, "E26.27.6", {"start": v(-29.91, -96.46) * mm, "end": v(-31.2, -96.04) * mm});
            skLineSegment(sketch, "E26.27.7", {"start": v(-28.58, -87.95) * mm, "end": v(-31.2, -96.04) * mm, "construction": true});
            skLineSegment(sketch, "E26.28.0", {"start": v(-20.56, -90.18) * mm, "end": v(-19.23, -90.46) * mm});
            skLineSegment(sketch, "E26.28.1", {"start": v(-22.32, -98.5) * mm, "end": v(-21, -98.77) * mm});
            skLineSegment(sketch, "E26.28.2", {"start": v(-20.56, -90.18) * mm, "end": v(-22.32, -98.5) * mm});
            skLineSegment(sketch, "E26.28.3", {"start": v(-22.03, -94.2) * mm, "end": v(-18.68, -94.92) * mm, "construction": true});
            skLineSegment(sketch, "E26.28.4", {"start": v(-17.9, -90.74) * mm, "end": v(-19.23, -90.46) * mm});
            skLineSegment(sketch, "E26.28.5", {"start": v(-17.9, -90.74) * mm, "end": v(-19.67, -99.06) * mm});
            skLineSegment(sketch, "E26.28.6", {"start": v(-19.67, -99.06) * mm, "end": v(-21, -98.77) * mm});
            skLineSegment(sketch, "E26.28.7", {"start": v(-19.23, -90.46) * mm, "end": v(-21, -98.77) * mm, "construction": true});
            skLineSegment(sketch, "E26.29.0", {"start": v(-11.02, -91.83) * mm, "end": v(-9.67, -91.97) * mm});
            skLineSegment(sketch, "E26.29.1", {"start": v(-11.9, -100.28) * mm, "end": v(-10.56, -100.43) * mm});
            skLineSegment(sketch, "E26.29.2", {"start": v(-11.02, -91.83) * mm, "end": v(-11.9, -100.28) * mm});
            skLineSegment(sketch, "E26.29.3", {"start": v(-12.06, -96) * mm, "end": v(-8.66, -96.35) * mm, "construction": true});
            skLineSegment(sketch, "E26.29.4", {"start": v(-8.32, -92.12) * mm, "end": v(-9.67, -91.97) * mm});
            skLineSegment(sketch, "E26.29.5", {"start": v(-8.32, -92.12) * mm, "end": v(-9.2, -100.57) * mm});
            skLineSegment(sketch, "E26.29.6", {"start": v(-9.2, -100.57) * mm, "end": v(-10.56, -100.43) * mm});
            skLineSegment(sketch, "E26.29.7", {"start": v(-9.67, -91.97) * mm, "end": v(-10.56, -100.43) * mm, "construction": true});
            skLineSegment(sketch, "E26.30.0", {"start": v(-1.36, -92.48) * mm, "end": v(0, -92.48) * mm});
            skLineSegment(sketch, "E26.30.1", {"start": v(-1.36, -100.98) * mm, "end": v(0, -100.98) * mm});
            skLineSegment(sketch, "E26.30.2", {"start": v(-1.36, -92.48) * mm, "end": v(-1.36, -100.98) * mm});
            skLineSegment(sketch, "E26.30.3", {"start": v(-1.96, -96.73) * mm, "end": v(1.46, -96.73) * mm, "construction": true});
            skLineSegment(sketch, "E26.30.4", {"start": v(1.36, -92.48) * mm, "end": v(0, -92.48) * mm});
            skLineSegment(sketch, "E26.30.5", {"start": v(1.36, -92.48) * mm, "end": v(1.36, -100.98) * mm});
            skLineSegment(sketch, "E26.30.6", {"start": v(1.36, -100.98) * mm, "end": v(0, -100.98) * mm});
            skLineSegment(sketch, "E26.30.7", {"start": v(0, -92.48) * mm, "end": v(0, -100.98) * mm, "construction": true});
            skLineSegment(sketch, "E26.31.0", {"start": v(8.32, -92.12) * mm, "end": v(9.67, -91.97) * mm});
            skLineSegment(sketch, "E26.31.1", {"start": v(9.2, -100.57) * mm, "end": v(10.56, -100.43) * mm});
            skLineSegment(sketch, "E26.31.2", {"start": v(8.32, -92.12) * mm, "end": v(9.2, -100.57) * mm});
            skLineSegment(sketch, "E26.31.3", {"start": v(8.16, -96.4) * mm, "end": v(11.56, -96.05) * mm, "construction": true});
            skLineSegment(sketch, "E26.31.4", {"start": v(11.02, -91.83) * mm, "end": v(9.67, -91.97) * mm});
            skLineSegment(sketch, "E26.31.5", {"start": v(11.02, -91.83) * mm, "end": v(11.9, -100.28) * mm});
            skLineSegment(sketch, "E26.31.6", {"start": v(11.9, -100.28) * mm, "end": v(10.56, -100.43) * mm});
            skLineSegment(sketch, "E26.31.7", {"start": v(9.67, -91.97) * mm, "end": v(10.56, -100.43) * mm, "construction": true});
            skLineSegment(sketch, "E26.32.0", {"start": v(17.9, -90.74) * mm, "end": v(19.23, -90.46) * mm});
            skLineSegment(sketch, "E26.32.1", {"start": v(19.67, -99.06) * mm, "end": v(21, -98.77) * mm});
            skLineSegment(sketch, "E26.32.2", {"start": v(17.9, -90.74) * mm, "end": v(19.67, -99.06) * mm});
            skLineSegment(sketch, "E26.32.3", {"start": v(18.2, -95.02) * mm, "end": v(21.54, -94.31) * mm, "construction": true});
            skLineSegment(sketch, "E26.32.4", {"start": v(20.56, -90.18) * mm, "end": v(19.23, -90.46) * mm});
            skLineSegment(sketch, "E26.32.5", {"start": v(20.56, -90.18) * mm, "end": v(22.32, -98.5) * mm});
            skLineSegment(sketch, "E26.32.6", {"start": v(22.32, -98.5) * mm, "end": v(21, -98.77) * mm});
            skLineSegment(sketch, "E26.32.7", {"start": v(19.23, -90.46) * mm, "end": v(21, -98.77) * mm, "construction": true});
            skLineSegment(sketch, "E26.33.0", {"start": v(27.29, -88.37) * mm, "end": v(28.58, -87.95) * mm});
            skLineSegment(sketch, "E26.33.1", {"start": v(29.91, -96.46) * mm, "end": v(31.2, -96.04) * mm});
            skLineSegment(sketch, "E26.33.2", {"start": v(27.29, -88.37) * mm, "end": v(29.91, -96.46) * mm});
            skLineSegment(sketch, "E26.33.3", {"start": v(28.02, -92.6) * mm, "end": v(31.28, -91.54) * mm, "construction": true});
            skLineSegment(sketch, "E26.33.4", {"start": v(29.87, -87.53) * mm, "end": v(28.58, -87.95) * mm});
            skLineSegment(sketch, "E26.33.5", {"start": v(29.87, -87.53) * mm, "end": v(32.5, -95.62) * mm});
            skLineSegment(sketch, "E26.33.6", {"start": v(32.5, -95.62) * mm, "end": v(31.2, -96.04) * mm});
            skLineSegment(sketch, "E26.33.7", {"start": v(28.58, -87.95) * mm, "end": v(31.2, -96.04) * mm, "construction": true});
            skLineSegment(sketch, "E26.34.0", {"start": v(36.37, -85.04) * mm, "end": v(37.62, -84.48) * mm});
            skLineSegment(sketch, "E26.34.1", {"start": v(39.83, -92.8) * mm, "end": v(41.07, -92.25) * mm});
            skLineSegment(sketch, "E26.34.2", {"start": v(36.37, -85.04) * mm, "end": v(39.83, -92.8) * mm});
            skLineSegment(sketch, "E26.34.3", {"start": v(37.55, -89.17) * mm, "end": v(40.68, -87.77) * mm, "construction": true});
            skLineSegment(sketch, "E26.34.4", {"start": v(38.86, -83.93) * mm, "end": v(37.62, -84.48) * mm});
            skLineSegment(sketch, "E26.34.5", {"start": v(38.86, -83.93) * mm, "end": v(42.31, -91.7) * mm});
            skLineSegment(sketch, "E26.34.6", {"start": v(42.31, -91.7) * mm, "end": v(41.07, -92.25) * mm});
            skLineSegment(sketch, "E26.34.7", {"start": v(37.62, -84.48) * mm, "end": v(41.07, -92.25) * mm, "construction": true});
            skLineSegment(sketch, "E26.35.0", {"start": v(45.06, -80.77) * mm, "end": v(46.24, -80.1) * mm});
            skLineSegment(sketch, "E26.35.1", {"start": v(49.31, -88.13) * mm, "end": v(50.49, -87.45) * mm});
            skLineSegment(sketch, "E26.35.2", {"start": v(45.06, -80.77) * mm, "end": v(49.31, -88.13) * mm});
            skLineSegment(sketch, "E26.35.3", {"start": v(46.67, -84.75) * mm, "end": v(49.63, -83.04) * mm, "construction": true});
            skLineSegment(sketch, "E26.35.4", {"start": v(47.42, -79.41) * mm, "end": v(46.24, -80.1) * mm});
            skLineSegment(sketch, "E26.35.5", {"start": v(47.42, -79.41) * mm, "end": v(51.67, -86.77) * mm});
            skLineSegment(sketch, "E26.35.6", {"start": v(51.67, -86.77) * mm, "end": v(50.49, -87.45) * mm});
            skLineSegment(sketch, "E26.35.7", {"start": v(46.24, -80.1) * mm, "end": v(50.49, -87.45) * mm, "construction": true});
            skLineSegment(sketch, "E26.36.0", {"start": v(53.26, -75.62) * mm, "end": v(54.36, -74.82) * mm});
            skLineSegment(sketch, "E26.36.1", {"start": v(58.26, -82.5) * mm, "end": v(59.35, -81.7) * mm});
            skLineSegment(sketch, "E26.36.2", {"start": v(53.26, -75.62) * mm, "end": v(58.26, -82.5) * mm});
            skLineSegment(sketch, "E26.36.3", {"start": v(55.27, -79.4) * mm, "end": v(58.04, -77.4) * mm, "construction": true});
            skLineSegment(sketch, "E26.36.4", {"start": v(55.46, -74.02) * mm, "end": v(54.36, -74.82) * mm});
            skLineSegment(sketch, "E26.36.5", {"start": v(55.46, -74.02) * mm, "end": v(60.45, -80.9) * mm});
            skLineSegment(sketch, "E26.36.6", {"start": v(60.45, -80.9) * mm, "end": v(59.35, -81.7) * mm});
            skLineSegment(sketch, "E26.36.7", {"start": v(54.36, -74.82) * mm, "end": v(59.35, -81.7) * mm, "construction": true});
            skLineSegment(sketch, "E26.37.0", {"start": v(60.87, -69.63) * mm, "end": v(61.88, -68.73) * mm});
            skLineSegment(sketch, "E26.37.1", {"start": v(66.56, -75.95) * mm, "end": v(67.57, -75.04) * mm});
            skLineSegment(sketch, "E26.37.2", {"start": v(60.87, -69.63) * mm, "end": v(66.56, -75.95) * mm});
            skLineSegment(sketch, "E26.37.3", {"start": v(63.27, -73.2) * mm, "end": v(65.8, -70.9) * mm, "construction": true});
            skLineSegment(sketch, "E26.37.4", {"start": v(62.9, -67.82) * mm, "end": v(61.88, -68.73) * mm});
            skLineSegment(sketch, "E26.37.5", {"start": v(62.9, -67.82) * mm, "end": v(68.58, -74.13) * mm});
            skLineSegment(sketch, "E26.37.6", {"start": v(68.58, -74.13) * mm, "end": v(67.57, -75.04) * mm});
            skLineSegment(sketch, "E26.37.7", {"start": v(61.88, -68.73) * mm, "end": v(67.57, -75.04) * mm, "construction": true});
            skLineSegment(sketch, "E26.38.0", {"start": v(67.82, -62.9) * mm, "end": v(68.73, -61.88) * mm});
            skLineSegment(sketch, "E26.38.1", {"start": v(74.13, -68.58) * mm, "end": v(75.04, -67.57) * mm});
            skLineSegment(sketch, "E26.38.2", {"start": v(67.82, -62.9) * mm, "end": v(74.13, -68.58) * mm});
            skLineSegment(sketch, "E26.38.3", {"start": v(70.57, -66.18) * mm, "end": v(72.86, -63.64) * mm, "construction": true});
            skLineSegment(sketch, "E26.38.4", {"start": v(69.63, -60.87) * mm, "end": v(68.73, -61.88) * mm});
            skLineSegment(sketch, "E26.38.5", {"start": v(69.63, -60.87) * mm, "end": v(75.95, -66.56) * mm});
            skLineSegment(sketch, "E26.38.6", {"start": v(75.95, -66.56) * mm, "end": v(75.04, -67.57) * mm});
            skLineSegment(sketch, "E26.38.7", {"start": v(68.73, -61.88) * mm, "end": v(75.04, -67.57) * mm, "construction": true});
            skLineSegment(sketch, "E26.39.0", {"start": v(74.02, -55.46) * mm, "end": v(74.82, -54.36) * mm});
            skLineSegment(sketch, "E26.39.1", {"start": v(80.9, -60.45) * mm, "end": v(81.7, -59.35) * mm});
            skLineSegment(sketch, "E26.39.2", {"start": v(74.02, -55.46) * mm, "end": v(80.9, -60.45) * mm});
            skLineSegment(sketch, "E26.39.3", {"start": v(77.1, -58.44) * mm, "end": v(79.11, -55.68) * mm, "construction": true});
            skLineSegment(sketch, "E26.39.4", {"start": v(75.62, -53.26) * mm, "end": v(74.82, -54.36) * mm});
            skLineSegment(sketch, "E26.39.5", {"start": v(75.62, -53.26) * mm, "end": v(82.5, -58.26) * mm});
            skLineSegment(sketch, "E26.39.6", {"start": v(82.5, -58.26) * mm, "end": v(81.7, -59.35) * mm});
            skLineSegment(sketch, "E26.39.7", {"start": v(74.82, -54.36) * mm, "end": v(81.7, -59.35) * mm, "construction": true});
            skLineSegment(sketch, "E26.40.0", {"start": v(79.41, -47.42) * mm, "end": v(80.1, -46.24) * mm});
            skLineSegment(sketch, "E26.40.1", {"start": v(86.77, -51.67) * mm, "end": v(87.45, -50.5) * mm});
            skLineSegment(sketch, "E26.40.2", {"start": v(79.41, -47.42) * mm, "end": v(86.77, -51.67) * mm});
            skLineSegment(sketch, "E26.40.3", {"start": v(82.79, -50.06) * mm, "end": v(84.5, -47.1) * mm, "construction": true});
            skLineSegment(sketch, "E26.40.4", {"start": v(80.77, -45.06) * mm, "end": v(80.1, -46.24) * mm});
            skLineSegment(sketch, "E26.40.5", {"start": v(80.77, -45.06) * mm, "end": v(88.13, -49.31) * mm});
            skLineSegment(sketch, "E26.40.6", {"start": v(88.13, -49.31) * mm, "end": v(87.45, -50.5) * mm});
            skLineSegment(sketch, "E26.40.7", {"start": v(80.1, -46.24) * mm, "end": v(87.45, -50.5) * mm, "construction": true});
            skLineSegment(sketch, "E26.41.0", {"start": v(83.93, -38.86) * mm, "end": v(84.48, -37.62) * mm});
            skLineSegment(sketch, "E26.41.1", {"start": v(91.7, -42.31) * mm, "end": v(92.25, -41.07) * mm});
            skLineSegment(sketch, "E26.41.2", {"start": v(83.93, -38.86) * mm, "end": v(91.7, -42.31) * mm});
            skLineSegment(sketch, "E26.41.3", {"start": v(87.57, -41.14) * mm, "end": v(88.96, -38) * mm, "construction": true});
            skLineSegment(sketch, "E26.41.4", {"start": v(85.04, -36.37) * mm, "end": v(84.48, -37.62) * mm});
            skLineSegment(sketch, "E26.41.5", {"start": v(85.04, -36.37) * mm, "end": v(92.8, -39.83) * mm});
            skLineSegment(sketch, "E26.41.6", {"start": v(92.8, -39.83) * mm, "end": v(92.25, -41.07) * mm});
            skLineSegment(sketch, "E26.41.7", {"start": v(84.48, -37.62) * mm, "end": v(92.25, -41.07) * mm, "construction": true});
            skLineSegment(sketch, "E26.42.0", {"start": v(87.53, -29.87) * mm, "end": v(87.95, -28.58) * mm});
            skLineSegment(sketch, "E26.42.1", {"start": v(95.62, -32.5) * mm, "end": v(96.04, -31.2) * mm});
            skLineSegment(sketch, "E26.42.2", {"start": v(87.53, -29.87) * mm, "end": v(95.62, -32.5) * mm});
            skLineSegment(sketch, "E26.42.3", {"start": v(91.39, -31.76) * mm, "end": v(92.45, -28.5) * mm, "construction": true});
            skLineSegment(sketch, "E26.42.4", {"start": v(88.37, -27.29) * mm, "end": v(87.95, -28.58) * mm});
            skLineSegment(sketch, "E26.42.5", {"start": v(88.37, -27.29) * mm, "end": v(96.46, -29.91) * mm});
            skLineSegment(sketch, "E26.42.6", {"start": v(96.46, -29.91) * mm, "end": v(96.04, -31.2) * mm});
            skLineSegment(sketch, "E26.42.7", {"start": v(87.95, -28.58) * mm, "end": v(96.04, -31.2) * mm, "construction": true});
            skLineSegment(sketch, "E26.43.0", {"start": v(90.18, -20.56) * mm, "end": v(90.46, -19.23) * mm});
            skLineSegment(sketch, "E26.43.1", {"start": v(98.5, -22.32) * mm, "end": v(98.77, -21) * mm});
            skLineSegment(sketch, "E26.43.2", {"start": v(90.18, -20.56) * mm, "end": v(98.5, -22.32) * mm});
            skLineSegment(sketch, "E26.43.3", {"start": v(94.2, -22.03) * mm, "end": v(94.92, -18.68) * mm, "construction": true});
            skLineSegment(sketch, "E26.43.4", {"start": v(90.74, -17.9) * mm, "end": v(90.46, -19.23) * mm});
            skLineSegment(sketch, "E26.43.5", {"start": v(90.74, -17.9) * mm, "end": v(99.06, -19.67) * mm});
            skLineSegment(sketch, "E26.43.6", {"start": v(99.06, -19.67) * mm, "end": v(98.77, -21) * mm});
            skLineSegment(sketch, "E26.43.7", {"start": v(90.46, -19.23) * mm, "end": v(98.77, -21) * mm, "construction": true});
            skLineSegment(sketch, "E26.44.0", {"start": v(91.83, -11.02) * mm, "end": v(91.97, -9.67) * mm});
            skLineSegment(sketch, "E26.44.1", {"start": v(100.28, -11.9) * mm, "end": v(100.43, -10.56) * mm});
            skLineSegment(sketch, "E26.44.2", {"start": v(91.83, -11.02) * mm, "end": v(100.28, -11.9) * mm});
            skLineSegment(sketch, "E26.44.3", {"start": v(96, -12.06) * mm, "end": v(96.35, -8.66) * mm, "construction": true});
            skLineSegment(sketch, "E26.44.4", {"start": v(92.12, -8.32) * mm, "end": v(91.97, -9.67) * mm});
            skLineSegment(sketch, "E26.44.5", {"start": v(92.12, -8.32) * mm, "end": v(100.57, -9.2) * mm});
            skLineSegment(sketch, "E26.44.6", {"start": v(100.57, -9.2) * mm, "end": v(100.43, -10.56) * mm});
            skLineSegment(sketch, "E26.44.7", {"start": v(91.97, -9.67) * mm, "end": v(100.43, -10.56) * mm, "construction": true});
            skLineSegment(sketch, "E26.45.0", {"start": v(92.48, -1.36) * mm, "end": v(92.48, 0) * mm});
            skLineSegment(sketch, "E26.45.1", {"start": v(100.98, -1.36) * mm, "end": v(100.98, 0) * mm});
            skLineSegment(sketch, "E26.45.2", {"start": v(92.48, -1.36) * mm, "end": v(100.98, -1.36) * mm});
            skLineSegment(sketch, "E26.45.3", {"start": v(96.73, -1.96) * mm, "end": v(96.73, 1.46) * mm, "construction": true});
            skLineSegment(sketch, "E26.45.4", {"start": v(92.48, 1.36) * mm, "end": v(92.48, 0) * mm});
            skLineSegment(sketch, "E26.45.5", {"start": v(92.48, 1.36) * mm, "end": v(100.98, 1.36) * mm});
            skLineSegment(sketch, "E26.45.6", {"start": v(100.98, 1.36) * mm, "end": v(100.98, 0) * mm});
            skLineSegment(sketch, "E26.45.7", {"start": v(92.48, 0) * mm, "end": v(100.98, 0) * mm, "construction": true});
            skLineSegment(sketch, "E26.46.0", {"start": v(92.12, 8.32) * mm, "end": v(91.97, 9.67) * mm});
            skLineSegment(sketch, "E26.46.1", {"start": v(100.57, 9.2) * mm, "end": v(100.43, 10.56) * mm});
            skLineSegment(sketch, "E26.46.2", {"start": v(92.12, 8.32) * mm, "end": v(100.57, 9.2) * mm});
            skLineSegment(sketch, "E26.46.3", {"start": v(96.4, 8.16) * mm, "end": v(96.05, 11.56) * mm, "construction": true});
            skLineSegment(sketch, "E26.46.4", {"start": v(91.83, 11.02) * mm, "end": v(91.97, 9.67) * mm});
            skLineSegment(sketch, "E26.46.5", {"start": v(91.83, 11.02) * mm, "end": v(100.28, 11.9) * mm});
            skLineSegment(sketch, "E26.46.6", {"start": v(100.28, 11.9) * mm, "end": v(100.43, 10.56) * mm});
            skLineSegment(sketch, "E26.46.7", {"start": v(91.97, 9.67) * mm, "end": v(100.43, 10.56) * mm, "construction": true});
            skLineSegment(sketch, "E26.47.0", {"start": v(90.74, 17.9) * mm, "end": v(90.46, 19.23) * mm});
            skLineSegment(sketch, "E26.47.1", {"start": v(99.06, 19.67) * mm, "end": v(98.77, 21) * mm});
            skLineSegment(sketch, "E26.47.2", {"start": v(90.74, 17.9) * mm, "end": v(99.06, 19.67) * mm});
            skLineSegment(sketch, "E26.47.3", {"start": v(95.02, 18.2) * mm, "end": v(94.31, 21.54) * mm, "construction": true});
            skLineSegment(sketch, "E26.47.4", {"start": v(90.18, 20.56) * mm, "end": v(90.46, 19.23) * mm});
            skLineSegment(sketch, "E26.47.5", {"start": v(90.18, 20.56) * mm, "end": v(98.5, 22.32) * mm});
            skLineSegment(sketch, "E26.47.6", {"start": v(98.5, 22.32) * mm, "end": v(98.77, 21) * mm});
            skLineSegment(sketch, "E26.47.7", {"start": v(90.46, 19.23) * mm, "end": v(98.77, 21) * mm, "construction": true});
            skLineSegment(sketch, "E26.48.0", {"start": v(88.37, 27.29) * mm, "end": v(87.95, 28.58) * mm});
            skLineSegment(sketch, "E26.48.1", {"start": v(96.46, 29.91) * mm, "end": v(96.04, 31.2) * mm});
            skLineSegment(sketch, "E26.48.2", {"start": v(88.37, 27.29) * mm, "end": v(96.46, 29.91) * mm});
            skLineSegment(sketch, "E26.48.3", {"start": v(92.6, 28.02) * mm, "end": v(91.54, 31.28) * mm, "construction": true});
            skLineSegment(sketch, "E26.48.4", {"start": v(87.53, 29.87) * mm, "end": v(87.95, 28.58) * mm});
            skLineSegment(sketch, "E26.48.5", {"start": v(87.53, 29.87) * mm, "end": v(95.62, 32.5) * mm});
            skLineSegment(sketch, "E26.48.6", {"start": v(95.62, 32.5) * mm, "end": v(96.04, 31.2) * mm});
            skLineSegment(sketch, "E26.48.7", {"start": v(87.95, 28.58) * mm, "end": v(96.04, 31.2) * mm, "construction": true});
            skLineSegment(sketch, "E26.49.0", {"start": v(85.04, 36.37) * mm, "end": v(84.48, 37.62) * mm});
            skLineSegment(sketch, "E26.49.1", {"start": v(92.8, 39.83) * mm, "end": v(92.25, 41.07) * mm});
            skLineSegment(sketch, "E26.49.2", {"start": v(85.04, 36.37) * mm, "end": v(92.8, 39.83) * mm});
            skLineSegment(sketch, "E26.49.3", {"start": v(89.17, 37.55) * mm, "end": v(87.77, 40.68) * mm, "construction": true});
            skLineSegment(sketch, "E26.49.4", {"start": v(83.93, 38.86) * mm, "end": v(84.48, 37.62) * mm});
            skLineSegment(sketch, "E26.49.5", {"start": v(83.93, 38.86) * mm, "end": v(91.7, 42.31) * mm});
            skLineSegment(sketch, "E26.49.6", {"start": v(91.7, 42.31) * mm, "end": v(92.25, 41.07) * mm});
            skLineSegment(sketch, "E26.49.7", {"start": v(84.48, 37.62) * mm, "end": v(92.25, 41.07) * mm, "construction": true});
            skLineSegment(sketch, "E26.50.0", {"start": v(80.77, 45.06) * mm, "end": v(80.1, 46.24) * mm});
            skLineSegment(sketch, "E26.50.1", {"start": v(88.13, 49.31) * mm, "end": v(87.45, 50.49) * mm});
            skLineSegment(sketch, "E26.50.2", {"start": v(80.77, 45.06) * mm, "end": v(88.13, 49.31) * mm});
            skLineSegment(sketch, "E26.50.3", {"start": v(84.75, 46.67) * mm, "end": v(83.04, 49.63) * mm, "construction": true});
            skLineSegment(sketch, "E26.50.4", {"start": v(79.41, 47.42) * mm, "end": v(80.1, 46.24) * mm});
            skLineSegment(sketch, "E26.50.5", {"start": v(79.41, 47.42) * mm, "end": v(86.77, 51.67) * mm});
            skLineSegment(sketch, "E26.50.6", {"start": v(86.77, 51.67) * mm, "end": v(87.45, 50.49) * mm});
            skLineSegment(sketch, "E26.50.7", {"start": v(80.1, 46.24) * mm, "end": v(87.45, 50.49) * mm, "construction": true});
            skLineSegment(sketch, "E26.51.0", {"start": v(75.62, 53.26) * mm, "end": v(74.82, 54.36) * mm});
            skLineSegment(sketch, "E26.51.1", {"start": v(82.5, 58.26) * mm, "end": v(81.7, 59.35) * mm});
            skLineSegment(sketch, "E26.51.2", {"start": v(75.62, 53.26) * mm, "end": v(82.5, 58.26) * mm});
            skLineSegment(sketch, "E26.51.3", {"start": v(79.4, 55.27) * mm, "end": v(77.4, 58.04) * mm, "construction": true});
            skLineSegment(sketch, "E26.51.4", {"start": v(74.02, 55.46) * mm, "end": v(74.82, 54.36) * mm});
            skLineSegment(sketch, "E26.51.5", {"start": v(74.02, 55.46) * mm, "end": v(80.9, 60.45) * mm});
            skLineSegment(sketch, "E26.51.6", {"start": v(80.9, 60.45) * mm, "end": v(81.7, 59.35) * mm});
            skLineSegment(sketch, "E26.51.7", {"start": v(74.82, 54.36) * mm, "end": v(81.7, 59.35) * mm, "construction": true});
            skLineSegment(sketch, "E26.52.0", {"start": v(69.63, 60.87) * mm, "end": v(68.73, 61.88) * mm});
            skLineSegment(sketch, "E26.52.1", {"start": v(75.95, 66.56) * mm, "end": v(75.04, 67.57) * mm});
            skLineSegment(sketch, "E26.52.2", {"start": v(69.63, 60.87) * mm, "end": v(75.95, 66.56) * mm});
            skLineSegment(sketch, "E26.52.3", {"start": v(73.2, 63.27) * mm, "end": v(70.9, 65.8) * mm, "construction": true});
            skLineSegment(sketch, "E26.52.4", {"start": v(67.82, 62.9) * mm, "end": v(68.73, 61.88) * mm});
            skLineSegment(sketch, "E26.52.5", {"start": v(67.82, 62.9) * mm, "end": v(74.13, 68.58) * mm});
            skLineSegment(sketch, "E26.52.6", {"start": v(74.13, 68.58) * mm, "end": v(75.04, 67.57) * mm});
            skLineSegment(sketch, "E26.52.7", {"start": v(68.73, 61.88) * mm, "end": v(75.04, 67.57) * mm, "construction": true});
            skLineSegment(sketch, "E26.53.0", {"start": v(62.9, 67.82) * mm, "end": v(61.88, 68.73) * mm});
            skLineSegment(sketch, "E26.53.1", {"start": v(68.58, 74.13) * mm, "end": v(67.57, 75.04) * mm});
            skLineSegment(sketch, "E26.53.2", {"start": v(62.9, 67.82) * mm, "end": v(68.58, 74.13) * mm});
            skLineSegment(sketch, "E26.53.3", {"start": v(66.18, 70.57) * mm, "end": v(63.64, 72.86) * mm, "construction": true});
            skLineSegment(sketch, "E26.53.4", {"start": v(60.87, 69.63) * mm, "end": v(61.88, 68.73) * mm});
            skLineSegment(sketch, "E26.53.5", {"start": v(60.87, 69.63) * mm, "end": v(66.56, 75.95) * mm});
            skLineSegment(sketch, "E26.53.6", {"start": v(66.56, 75.95) * mm, "end": v(67.57, 75.04) * mm});
            skLineSegment(sketch, "E26.53.7", {"start": v(61.88, 68.73) * mm, "end": v(67.57, 75.04) * mm, "construction": true});
            skLineSegment(sketch, "E26.54.0", {"start": v(55.46, 74.02) * mm, "end": v(54.36, 74.82) * mm});
            skLineSegment(sketch, "E26.54.1", {"start": v(60.45, 80.9) * mm, "end": v(59.35, 81.7) * mm});
            skLineSegment(sketch, "E26.54.2", {"start": v(55.46, 74.02) * mm, "end": v(60.45, 80.9) * mm});
            skLineSegment(sketch, "E26.54.3", {"start": v(58.44, 77.1) * mm, "end": v(55.68, 79.11) * mm, "construction": true});
            skLineSegment(sketch, "E26.54.4", {"start": v(53.26, 75.62) * mm, "end": v(54.36, 74.82) * mm});
            skLineSegment(sketch, "E26.54.5", {"start": v(53.26, 75.62) * mm, "end": v(58.26, 82.5) * mm});
            skLineSegment(sketch, "E26.54.6", {"start": v(58.26, 82.5) * mm, "end": v(59.35, 81.7) * mm});
            skLineSegment(sketch, "E26.54.7", {"start": v(54.36, 74.82) * mm, "end": v(59.35, 81.7) * mm, "construction": true});
            skLineSegment(sketch, "E26.55.0", {"start": v(47.42, 79.41) * mm, "end": v(46.24, 80.1) * mm});
            skLineSegment(sketch, "E26.55.1", {"start": v(51.67, 86.77) * mm, "end": v(50.49, 87.45) * mm});
            skLineSegment(sketch, "E26.55.2", {"start": v(47.42, 79.41) * mm, "end": v(51.67, 86.77) * mm});
            skLineSegment(sketch, "E26.55.3", {"start": v(50.06, 82.79) * mm, "end": v(47.1, 84.5) * mm, "construction": true});
            skLineSegment(sketch, "E26.55.4", {"start": v(45.06, 80.77) * mm, "end": v(46.24, 80.1) * mm});
            skLineSegment(sketch, "E26.55.5", {"start": v(45.06, 80.77) * mm, "end": v(49.31, 88.13) * mm});
            skLineSegment(sketch, "E26.55.6", {"start": v(49.31, 88.13) * mm, "end": v(50.49, 87.45) * mm});
            skLineSegment(sketch, "E26.55.7", {"start": v(46.24, 80.1) * mm, "end": v(50.49, 87.45) * mm, "construction": true});
            skLineSegment(sketch, "E26.56.0", {"start": v(38.86, 83.93) * mm, "end": v(37.62, 84.48) * mm});
            skLineSegment(sketch, "E26.56.1", {"start": v(42.31, 91.7) * mm, "end": v(41.07, 92.25) * mm});
            skLineSegment(sketch, "E26.56.2", {"start": v(38.86, 83.93) * mm, "end": v(42.31, 91.7) * mm});
            skLineSegment(sketch, "E26.56.3", {"start": v(41.14, 87.57) * mm, "end": v(38, 88.96) * mm, "construction": true});
            skLineSegment(sketch, "E26.56.4", {"start": v(36.37, 85.04) * mm, "end": v(37.62, 84.48) * mm});
            skLineSegment(sketch, "E26.56.5", {"start": v(36.37, 85.04) * mm, "end": v(39.83, 92.8) * mm});
            skLineSegment(sketch, "E26.56.6", {"start": v(39.83, 92.8) * mm, "end": v(41.07, 92.25) * mm});
            skLineSegment(sketch, "E26.56.7", {"start": v(37.62, 84.48) * mm, "end": v(41.07, 92.25) * mm, "construction": true});
            skLineSegment(sketch, "E26.57.0", {"start": v(29.87, 87.53) * mm, "end": v(28.58, 87.95) * mm});
            skLineSegment(sketch, "E26.57.1", {"start": v(32.5, 95.62) * mm, "end": v(31.2, 96.04) * mm});
            skLineSegment(sketch, "E26.57.2", {"start": v(29.87, 87.53) * mm, "end": v(32.5, 95.62) * mm});
            skLineSegment(sketch, "E26.57.3", {"start": v(31.76, 91.39) * mm, "end": v(28.5, 92.45) * mm, "construction": true});
            skLineSegment(sketch, "E26.57.4", {"start": v(27.29, 88.37) * mm, "end": v(28.58, 87.95) * mm});
            skLineSegment(sketch, "E26.57.5", {"start": v(27.29, 88.37) * mm, "end": v(29.91, 96.46) * mm});
            skLineSegment(sketch, "E26.57.6", {"start": v(29.91, 96.46) * mm, "end": v(31.2, 96.04) * mm});
            skLineSegment(sketch, "E26.57.7", {"start": v(28.58, 87.95) * mm, "end": v(31.2, 96.04) * mm, "construction": true});
            skLineSegment(sketch, "E26.58.0", {"start": v(20.56, 90.18) * mm, "end": v(19.23, 90.46) * mm});
            skLineSegment(sketch, "E26.58.1", {"start": v(22.32, 98.5) * mm, "end": v(21, 98.77) * mm});
            skLineSegment(sketch, "E26.58.2", {"start": v(20.56, 90.18) * mm, "end": v(22.32, 98.5) * mm});
            skLineSegment(sketch, "E26.58.3", {"start": v(22.03, 94.2) * mm, "end": v(18.68, 94.92) * mm, "construction": true});
            skLineSegment(sketch, "E26.58.4", {"start": v(17.9, 90.74) * mm, "end": v(19.23, 90.46) * mm});
            skLineSegment(sketch, "E26.58.5", {"start": v(17.9, 90.74) * mm, "end": v(19.67, 99.06) * mm});
            skLineSegment(sketch, "E26.58.6", {"start": v(19.67, 99.06) * mm, "end": v(21, 98.77) * mm});
            skLineSegment(sketch, "E26.58.7", {"start": v(19.23, 90.46) * mm, "end": v(21, 98.77) * mm, "construction": true});
            skLineSegment(sketch, "E26.59.0", {"start": v(11.02, 91.83) * mm, "end": v(9.67, 91.97) * mm});
            skLineSegment(sketch, "E26.59.1", {"start": v(11.9, 100.28) * mm, "end": v(10.56, 100.43) * mm});
            skLineSegment(sketch, "E26.59.2", {"start": v(11.02, 91.83) * mm, "end": v(11.9, 100.28) * mm});
            skLineSegment(sketch, "E26.59.3", {"start": v(12.06, 96) * mm, "end": v(8.66, 96.35) * mm, "construction": true});
            skLineSegment(sketch, "E26.59.4", {"start": v(8.32, 92.12) * mm, "end": v(9.67, 91.97) * mm});
            skLineSegment(sketch, "E26.59.5", {"start": v(8.32, 92.12) * mm, "end": v(9.2, 100.57) * mm});
            skLineSegment(sketch, "E26.59.6", {"start": v(9.2, 100.57) * mm, "end": v(10.56, 100.43) * mm});
            skLineSegment(sketch, "E26.59.7", {"start": v(9.67, 91.97) * mm, "end": v(10.56, 100.43) * mm, "construction": true});
            skPoint(sketch, "E26.center", {"position": v(0, 0) * mm});
            skSolve(sketch);
        }
        {
            var Q0;
            Q0=qSketchRegion(id+"F13",true);
            extrude(context, id + "F14", {"entities" : qUnion([Q0]), "operationType" : NewBodyOperationType.REMOVE, "depth" : 25 * mm, "offsetDistance" : 25 * mm, "hasSecondDirection" : true, "secondDirectionOppositeDirection" : false, "secondDirectionDepth" : 2 * mm});
        }
        {
            var Q0;
            Q0=makeQuery(id+"F1.opRevolve","SWEPT_FACE",FACE,{"disambiguationData":[OSD([sQuery(id+"F0.wireOp",EDGE,"E5")])]});
            var sketch = newSketch(context, id + "F15", { "sketchPlane" : qUnion([Q0])});
            skLineSegment(sketch, "E27", {"start": v(0, 0) * mm, "end": v(25.68, 95.85) * mm, "construction": true});
            skLineSegment(sketch, "E28", {"start": v(0, 0) * mm, "end": v(70.17, 70.17) * mm, "construction": true});
            skLineSegment(sketch, "E29", {"start": v(0, 0) * mm, "end": v(95.85, 25.68) * mm, "construction": true});
            skLineSegment(sketch, "E30", {"start": v(0, 0) * mm, "end": v(95.85, -25.68) * mm, "construction": true});
            skLineSegment(sketch, "E31", {"start": v(0, 0) * mm, "end": v(70.17, -70.17) * mm, "construction": true});
            skLineSegment(sketch, "E32", {"start": v(0, 0) * mm, "end": v(25.68, -95.85) * mm, "construction": true});
            skLineSegment(sketch, "E33", {"start": v(0, 0) * mm, "end": v(104.73, 0) * mm, "construction": true});
            skArc(sketch, "E34", {"start": v(22.25, -102.34) * mm, "mid": v(27.1, -101.16) * mm, "end": v(31.9, -99.75) * mm});
            skArc(sketch, "E35", {"start": v(21.47, -99.44) * mm, "mid": v(26.33, -98.26) * mm, "end": v(31.13, -96.85) * mm});
            skLineSegment(sketch, "E36", {"start": v(25.68, 95.85) * mm, "end": v(30.51, 94.55) * mm, "construction": true});
            skLineSegment(sketch, "E37.MirrorCS", {"start": v(25.68, 95.85) * mm, "end": v(20.85, 97.14) * mm, "construction": true});
            skLineSegment(sketch, "E38", {"start": v(21.47, 99.44) * mm, "end": v(22.25, 102.34) * mm});
            skLineSegment(sketch, "E39", {"start": v(31.13, 96.85) * mm, "end": v(31.9, 99.75) * mm});
            skLineSegment(sketch, "E40", {"start": v(70.17, 70.17) * mm, "end": v(73.7, 66.63) * mm, "construction": true});
            skLineSegment(sketch, "E41.MirrorCS", {"start": v(70.17, 70.17) * mm, "end": v(66.63, 73.7) * mm, "construction": true});
            skLineSegment(sketch, "E42", {"start": v(75.38, 68.31) * mm, "end": v(77.5, 70.44) * mm});
            skLineSegment(sketch, "E43", {"start": v(68.31, 75.38) * mm, "end": v(70.44, 77.5) * mm});
            skArc(sketch, "E44.trimOffspring", {"start": v(31.9, 99.75) * mm, "mid": v(27.1, 101.16) * mm, "end": v(22.25, 102.34) * mm});
            skArc(sketch, "E45.trimOffspring", {"start": v(31.13, 96.85) * mm, "mid": v(26.33, 98.26) * mm, "end": v(21.47, 99.44) * mm});
            skLineSegment(sketch, "E46", {"start": v(95.85, 25.68) * mm, "end": v(97.14, 20.85) * mm, "construction": true});
            skLineSegment(sketch, "E47.MirrorCS", {"start": v(95.85, 25.68) * mm, "end": v(94.55, 30.51) * mm, "construction": true});
            skLineSegment(sketch, "E48", {"start": v(96.85, 31.13) * mm, "end": v(99.75, 31.9) * mm});
            skLineSegment(sketch, "E49", {"start": v(99.44, 21.47) * mm, "end": v(102.34, 22.25) * mm});
            skArc(sketch, "E50.trimOffspring", {"start": v(75.38, 68.31) * mm, "mid": v(71.93, 71.93) * mm, "end": v(68.31, 75.38) * mm});
            skArc(sketch, "E51.trimOffspring", {"start": v(77.5, 70.44) * mm, "mid": v(74.06, 74.06) * mm, "end": v(70.44, 77.5) * mm});
            skLineSegment(sketch, "E52", {"start": v(95.85, -25.68) * mm, "end": v(94.55, -30.51) * mm, "construction": true});
            skLineSegment(sketch, "E53.MirrorCS", {"start": v(95.85, -25.68) * mm, "end": v(97.14, -20.85) * mm, "construction": true});
            skLineSegment(sketch, "E54", {"start": v(96.85, -31.13) * mm, "end": v(99.75, -31.9) * mm});
            skLineSegment(sketch, "E55", {"start": v(99.44, -21.47) * mm, "end": v(102.34, -22.25) * mm});
            skArc(sketch, "E56.trimOffspring", {"start": v(99.44, 21.47) * mm, "mid": v(98.26, 26.33) * mm, "end": v(96.85, 31.13) * mm});
            skArc(sketch, "E57.trimOffspring", {"start": v(102.34, 22.25) * mm, "mid": v(101.16, 27.1) * mm, "end": v(99.75, 31.9) * mm});
            skLineSegment(sketch, "E58", {"start": v(70.17, -70.17) * mm, "end": v(66.63, -73.7) * mm, "construction": true});
            skLineSegment(sketch, "E59.MirrorCS", {"start": v(70.17, -70.17) * mm, "end": v(73.7, -66.63) * mm, "construction": true});
            skLineSegment(sketch, "E60", {"start": v(75.38, -68.31) * mm, "end": v(77.5, -70.44) * mm});
            skLineSegment(sketch, "E61", {"start": v(68.31, -75.38) * mm, "end": v(70.44, -77.5) * mm});
            skArc(sketch, "E62.trimOffspring", {"start": v(99.75, -31.9) * mm, "mid": v(101.16, -27.1) * mm, "end": v(102.34, -22.25) * mm});
            skArc(sketch, "E63.trimOffspring", {"start": v(96.85, -31.13) * mm, "mid": v(98.26, -26.33) * mm, "end": v(99.44, -21.47) * mm});
            skLineSegment(sketch, "E64", {"start": v(25.68, -95.85) * mm, "end": v(20.85, -97.14) * mm, "construction": true});
            skLineSegment(sketch, "E65.MirrorCS", {"start": v(25.68, -95.85) * mm, "end": v(30.51, -94.55) * mm, "construction": true});
            skLineSegment(sketch, "E66", {"start": v(31.13, -96.85) * mm, "end": v(31.9, -99.75) * mm});
            skLineSegment(sketch, "E67", {"start": v(21.47, -99.44) * mm, "end": v(22.25, -102.34) * mm});
            skArc(sketch, "E68.trimOffspring", {"start": v(68.31, -75.38) * mm, "mid": v(71.93, -71.93) * mm, "end": v(75.38, -68.31) * mm});
            skArc(sketch, "E69.trimOffspring", {"start": v(70.44, -77.5) * mm, "mid": v(74.06, -74.06) * mm, "end": v(77.5, -70.44) * mm});
            skSolve(sketch);
        }
        {
            var Q0;
            Q0=makeQuery(id+"F15.imprint","IMPRINT",FACE,{"disambiguationData":[TD([[makeQuery(id+"F15.imprint","IMPRINT",EDGE,{"derivedFrom":sQuery(id+"F15.wireOp",EDGE,"E34")}),1.0]])]});
            var Q1;
            Q1=makeQuery(id+"F15.imprint","IMPRINT",FACE,{"disambiguationData":[TD([[makeQuery(id+"F15.imprint","IMPRINT",EDGE,{"derivedFrom":sQuery(id+"F15.wireOp",EDGE,"E60")}),-1.0]])]});
            var Q2;
            Q2=makeQuery(id+"F15.imprint","IMPRINT",FACE,{"disambiguationData":[TD([[makeQuery(id+"F15.imprint","IMPRINT",EDGE,{"derivedFrom":sQuery(id+"F15.wireOp",EDGE,"E54")}),1.0]])]});
            var Q3;
            Q3=makeQuery(id+"F15.imprint","IMPRINT",FACE,{"disambiguationData":[TD([[makeQuery(id+"F15.imprint","IMPRINT",EDGE,{"derivedFrom":sQuery(id+"F15.wireOp",EDGE,"E48")}),-1.0]])]});
            var Q4;
            Q4=makeQuery(id+"F15.imprint","IMPRINT",FACE,{"disambiguationData":[TD([[makeQuery(id+"F15.imprint","IMPRINT",EDGE,{"derivedFrom":sQuery(id+"F15.wireOp",EDGE,"E42")}),1.0]])]});
            var Q5;
            Q5=makeQuery(id+"F15.imprint","IMPRINT",FACE,{"disambiguationData":[TD([[makeQuery(id+"F15.imprint","IMPRINT",EDGE,{"derivedFrom":sQuery(id+"F15.wireOp",EDGE,"E38")}),-1.0]])]});
            extrude(context, id + "F16", {"entities" : qUnion([Q0, Q1, Q2, Q3, Q4, Q5]), "operationType" : NewBodyOperationType.ADD, "depth" : 5 * mm, "offsetDistance" : 25 * mm});
        }
        {
            var Q0;
            Q0=makeQuery(id+"F16.opExtrude","CAP_FACE",FACE,{"disambiguationData":[OSD([sQuery(id+"F15.wireOp",EDGE,"E34"),sQuery(id+"F15.wireOp",EDGE,"E35"),sQuery(id+"F15.wireOp",EDGE,"E66"),sQuery(id+"F15.wireOp",EDGE,"E67")])],"isStart":false});
            var sketch = newSketch(context, id + "F17", { "sketchPlane" : qUnion([Q0])});
            skLineSegment(sketch, "E70", {"start": v(27.24, -101.64) * mm, "end": v(26.2, -97.78) * mm});
            skLineSegment(sketch, "E71", {"start": v(26.2, -97.78) * mm, "end": v(27.17, -97.52) * mm});
            skLineSegment(sketch, "E72", {"start": v(27.17, -97.52) * mm, "end": v(28.2, -101.39) * mm});
            skLineSegment(sketch, "E73", {"start": v(28.2, -101.39) * mm, "end": v(27.24, -101.64) * mm});
            skLineSegment(sketch, "E74.1.0", {"start": v(75.12, -73.7) * mm, "end": v(74.4, -74.4) * mm});
            skLineSegment(sketch, "E74.1.1", {"start": v(72.29, -70.87) * mm, "end": v(75.12, -73.7) * mm});
            skLineSegment(sketch, "E74.1.2", {"start": v(71.58, -71.58) * mm, "end": v(72.29, -70.87) * mm});
            skLineSegment(sketch, "E74.1.3", {"start": v(74.4, -74.4) * mm, "end": v(71.58, -71.58) * mm});
            skLineSegment(sketch, "E74.2.0", {"start": v(101.9, -26.27) * mm, "end": v(101.64, -27.24) * mm});
            skLineSegment(sketch, "E74.2.1", {"start": v(98.04, -25.23) * mm, "end": v(101.9, -26.27) * mm});
            skLineSegment(sketch, "E74.2.2", {"start": v(97.78, -26.2) * mm, "end": v(98.04, -25.23) * mm});
            skLineSegment(sketch, "E74.2.3", {"start": v(101.64, -27.24) * mm, "end": v(97.78, -26.2) * mm});
            skLineSegment(sketch, "E74.3.0", {"start": v(101.39, 28.2) * mm, "end": v(101.64, 27.24) * mm});
            skLineSegment(sketch, "E74.3.1", {"start": v(97.52, 27.17) * mm, "end": v(101.39, 28.2) * mm});
            skLineSegment(sketch, "E74.3.2", {"start": v(97.78, 26.2) * mm, "end": v(97.52, 27.17) * mm});
            skLineSegment(sketch, "E74.3.3", {"start": v(101.64, 27.24) * mm, "end": v(97.78, 26.2) * mm});
            skLineSegment(sketch, "E74.4.0", {"start": v(73.7, 75.12) * mm, "end": v(74.4, 74.4) * mm});
            skLineSegment(sketch, "E74.4.1", {"start": v(70.87, 72.29) * mm, "end": v(73.7, 75.12) * mm});
            skLineSegment(sketch, "E74.4.2", {"start": v(71.58, 71.58) * mm, "end": v(70.87, 72.29) * mm});
            skLineSegment(sketch, "E74.4.3", {"start": v(74.4, 74.4) * mm, "end": v(71.58, 71.58) * mm});
            skLineSegment(sketch, "E74.5.0", {"start": v(26.27, 101.9) * mm, "end": v(27.24, 101.64) * mm});
            skLineSegment(sketch, "E74.5.1", {"start": v(25.23, 98.04) * mm, "end": v(26.27, 101.9) * mm});
            skLineSegment(sketch, "E74.5.2", {"start": v(26.2, 97.78) * mm, "end": v(25.23, 98.04) * mm});
            skLineSegment(sketch, "E74.5.3", {"start": v(27.24, 101.64) * mm, "end": v(26.2, 97.78) * mm});
            skLineSegment(sketch, "E74.6.0", {"start": v(-28.2, 101.39) * mm, "end": v(-27.24, 101.64) * mm});
            skLineSegment(sketch, "E74.6.1", {"start": v(-27.17, 97.52) * mm, "end": v(-28.2, 101.39) * mm});
            skLineSegment(sketch, "E74.6.2", {"start": v(-26.2, 97.78) * mm, "end": v(-27.17, 97.52) * mm});
            skLineSegment(sketch, "E74.6.3", {"start": v(-27.24, 101.64) * mm, "end": v(-26.2, 97.78) * mm});
            skLineSegment(sketch, "E74.7.0", {"start": v(-75.12, 73.7) * mm, "end": v(-74.4, 74.4) * mm});
            skLineSegment(sketch, "E74.7.1", {"start": v(-72.29, 70.87) * mm, "end": v(-75.12, 73.7) * mm});
            skLineSegment(sketch, "E74.7.2", {"start": v(-71.58, 71.58) * mm, "end": v(-72.29, 70.87) * mm});
            skLineSegment(sketch, "E74.7.3", {"start": v(-74.4, 74.4) * mm, "end": v(-71.58, 71.58) * mm});
            skLineSegment(sketch, "E74.8.0", {"start": v(-101.9, 26.27) * mm, "end": v(-101.64, 27.24) * mm});
            skLineSegment(sketch, "E74.8.1", {"start": v(-98.04, 25.23) * mm, "end": v(-101.9, 26.27) * mm});
            skLineSegment(sketch, "E74.8.2", {"start": v(-97.78, 26.2) * mm, "end": v(-98.04, 25.23) * mm});
            skLineSegment(sketch, "E74.8.3", {"start": v(-101.64, 27.24) * mm, "end": v(-97.78, 26.2) * mm});
            skLineSegment(sketch, "E74.9.0", {"start": v(-101.39, -28.2) * mm, "end": v(-101.64, -27.24) * mm});
            skLineSegment(sketch, "E74.9.1", {"start": v(-97.52, -27.17) * mm, "end": v(-101.39, -28.2) * mm});
            skLineSegment(sketch, "E74.9.2", {"start": v(-97.78, -26.2) * mm, "end": v(-97.52, -27.17) * mm});
            skLineSegment(sketch, "E74.9.3", {"start": v(-101.64, -27.24) * mm, "end": v(-97.78, -26.2) * mm});
            skLineSegment(sketch, "E74.10.0", {"start": v(-73.7, -75.12) * mm, "end": v(-74.4, -74.4) * mm});
            skLineSegment(sketch, "E74.10.1", {"start": v(-70.87, -72.29) * mm, "end": v(-73.7, -75.12) * mm});
            skLineSegment(sketch, "E74.10.2", {"start": v(-71.58, -71.58) * mm, "end": v(-70.87, -72.29) * mm});
            skLineSegment(sketch, "E74.10.3", {"start": v(-74.4, -74.4) * mm, "end": v(-71.58, -71.58) * mm});
            skLineSegment(sketch, "E74.11.0", {"start": v(-26.27, -101.9) * mm, "end": v(-27.24, -101.64) * mm});
            skLineSegment(sketch, "E74.11.1", {"start": v(-25.23, -98.04) * mm, "end": v(-26.27, -101.9) * mm});
            skLineSegment(sketch, "E74.11.2", {"start": v(-26.2, -97.78) * mm, "end": v(-25.23, -98.04) * mm});
            skLineSegment(sketch, "E74.11.3", {"start": v(-27.24, -101.64) * mm, "end": v(-26.2, -97.78) * mm});
            skPoint(sketch, "E74.center", {"position": v(0, 0) * mm});
            skSolve(sketch);
        }
        {
            var Q0;
            {var subQ5=makeQuery(id+"F16.opExtrude","CAP_EDGE",EDGE,{"disambiguationData":[OSD([sQuery(id+"F15.wireOp",EDGE,"E66")])],"isStart":false});Q0=makeQuery(id+"F17.imprint","IMPRINT",FACE,{"disambiguationData":[TD([[makeQuery(id+"F17.imprint","IMPRINT",EDGE,{"derivedFrom":subQ5}),-1.0]])]});}
            var Q1;
            {var subQ0=sQuery(id+"F17.wireOp",EDGE,"E70");var subQ1=makeQuery(id+"F16.opExtrude","CAP_EDGE",EDGE,{"disambiguationData":[OSD([sQuery(id+"F15.wireOp",EDGE,"E34")])],"isStart":false});var subQ2=makeQuery(id+"F17.imprint","INTERSECT",VERTEX,{"derivedFrom":[subQ1,subQ0]});Q1=makeQuery(id+"F17.imprint","IMPRINT",FACE,{"disambiguationData":[TD([[makeQuery(id+"F17.imprint","IMPRINT",EDGE,{"disambiguationData":[TD([[subQ2,-1.0]])],"derivedFrom":subQ0}),-1.0]])]});}
            var Q2;
            {var subQ5=makeQuery(id+"F16.opExtrude","CAP_EDGE",EDGE,{"disambiguationData":[OSD([sQuery(id+"F15.wireOp",EDGE,"E67")])],"isStart":false});Q2=makeQuery(id+"F17.imprint","IMPRINT",FACE,{"disambiguationData":[TD([[makeQuery(id+"F17.imprint","IMPRINT",EDGE,{"derivedFrom":subQ5}),1.0]])]});}
            extrude(context, id + "F18", {"entities" : qUnion([Q0, Q1, Q2]), "operationType" : NewBodyOperationType.ADD, "depth" : 5 * mm, "offsetDistance" : 25 * mm});
        }
        {
            var Q0;
            Q0=makeQuery(id+"F16.opExtrude","CAP_FACE",FACE,{"disambiguationData":[OSD([sQuery(id+"F15.wireOp",EDGE,"E60"),sQuery(id+"F15.wireOp",EDGE,"E61"),sQuery(id+"F15.wireOp",EDGE,"E68.trimOffspring"),sQuery(id+"F15.wireOp",EDGE,"E69.trimOffspring")])],"isStart":false});
            extrude(context, id + "F19", {"entities" : qUnion([Q0]), "operationType" : NewBodyOperationType.ADD, "depth" : 5 * mm, "offsetDistance" : 25 * mm});
        }
        {
            var Q0;
            Q0=makeQuery(id+"F16.opExtrude","CAP_FACE",FACE,{"disambiguationData":[OSD([sQuery(id+"F15.wireOp",EDGE,"E54"),sQuery(id+"F15.wireOp",EDGE,"E55"),sQuery(id+"F15.wireOp",EDGE,"E62.trimOffspring"),sQuery(id+"F15.wireOp",EDGE,"E63.trimOffspring")])],"isStart":false});
            extrude(context, id + "F20", {"entities" : qUnion([Q0]), "operationType" : NewBodyOperationType.ADD, "depth" : 5 * mm, "offsetDistance" : 25 * mm});
        }
        {
            var Q0;
            Q0=makeQuery(id+"F16.opExtrude","CAP_FACE",FACE,{"disambiguationData":[OSD([sQuery(id+"F15.wireOp",EDGE,"E48"),sQuery(id+"F15.wireOp",EDGE,"E49"),sQuery(id+"F15.wireOp",EDGE,"E56.trimOffspring"),sQuery(id+"F15.wireOp",EDGE,"E57.trimOffspring")])],"isStart":false});
            extrude(context, id + "F21", {"entities" : qUnion([Q0]), "operationType" : NewBodyOperationType.ADD, "depth" : 5 * mm, "offsetDistance" : 25 * mm});
        }
        {
            var Q0;
            Q0=makeQuery(id+"F16.opExtrude","CAP_FACE",FACE,{"disambiguationData":[OSD([sQuery(id+"F15.wireOp",EDGE,"E42"),sQuery(id+"F15.wireOp",EDGE,"E43"),sQuery(id+"F15.wireOp",EDGE,"E50.trimOffspring"),sQuery(id+"F15.wireOp",EDGE,"E51.trimOffspring")])],"isStart":false});
            extrude(context, id + "F22", {"entities" : qUnion([Q0]), "operationType" : NewBodyOperationType.ADD, "depth" : 5 * mm, "offsetDistance" : 25 * mm});
        }
        {
            var Q0;
            Q0=makeQuery(id+"F16.opExtrude","CAP_FACE",FACE,{"disambiguationData":[OSD([sQuery(id+"F15.wireOp",EDGE,"E38"),sQuery(id+"F15.wireOp",EDGE,"E39"),sQuery(id+"F15.wireOp",EDGE,"E44.trimOffspring"),sQuery(id+"F15.wireOp",EDGE,"E45.trimOffspring")])],"isStart":false});
            extrude(context, id + "F23", {"entities" : qUnion([Q0]), "operationType" : NewBodyOperationType.ADD, "depth" : 5 * mm, "offsetDistance" : 25 * mm});
        }
        {
            var Q0;
            Q0=makeQuery(id+"F17.imprint","IMPRINT",FACE,{"disambiguationData":[TD([[makeQuery(id+"F17.imprint","IMPRINT",EDGE,{"derivedFrom":sQuery(id+"F17.wireOp",EDGE,"E74.5.0")}),-1.0]])]});
            var Q1;
            Q1=sQuery(id+"F17.wireOp",EDGE,"E74.5.3");
            revolve(context, id + "F24", {"operationType" : NewBodyOperationType.REMOVE, "surfaceOperationType" : NewSurfaceOperationType.NEW, "entities" : qUnion([Q0]), "axis" : qUnion([Q1]), "revolveType" : RevolveType.FULL, "oppositeDirection" : true});
        }
        {
            var Q0;
            Q0=makeQuery(id+"F17.imprint","IMPRINT",FACE,{"disambiguationData":[TD([[makeQuery(id+"F17.imprint","IMPRINT",EDGE,{"derivedFrom":sQuery(id+"F17.wireOp",EDGE,"E74.4.0")}),-1.0]])]});
            var Q1;
            Q1=sQuery(id+"F17.wireOp",EDGE,"E74.4.3");
            revolve(context, id + "F25", {"operationType" : NewBodyOperationType.REMOVE, "surfaceOperationType" : NewSurfaceOperationType.NEW, "entities" : qUnion([Q0]), "axis" : qUnion([Q1]), "revolveType" : RevolveType.FULL, "oppositeDirection" : true});
        }
        {
            var Q0;
            Q0=makeQuery(id+"F17.imprint","IMPRINT",FACE,{"disambiguationData":[TD([[makeQuery(id+"F17.imprint","IMPRINT",EDGE,{"derivedFrom":sQuery(id+"F17.wireOp",EDGE,"E74.3.0")}),-1.0]])]});
            var Q1;
            Q1=sQuery(id+"F17.wireOp",EDGE,"E74.3.3");
            revolve(context, id + "F26", {"operationType" : NewBodyOperationType.REMOVE, "surfaceOperationType" : NewSurfaceOperationType.NEW, "entities" : qUnion([Q0]), "axis" : qUnion([Q1]), "revolveType" : RevolveType.FULL, "oppositeDirection" : true});
        }
        {
            var Q0;
            Q0=makeQuery(id+"F17.imprint","IMPRINT",FACE,{"disambiguationData":[TD([[makeQuery(id+"F17.imprint","IMPRINT",EDGE,{"derivedFrom":sQuery(id+"F17.wireOp",EDGE,"E74.2.0")}),-1.0]])]});
            var Q1;
            Q1=sQuery(id+"F17.wireOp",EDGE,"E74.2.3");
            revolve(context, id + "F27", {"operationType" : NewBodyOperationType.REMOVE, "surfaceOperationType" : NewSurfaceOperationType.NEW, "entities" : qUnion([Q0]), "axis" : qUnion([Q1]), "revolveType" : RevolveType.FULL, "oppositeDirection" : true});
        }
        {
            var Q0;
            Q0=makeQuery(id+"F17.imprint","IMPRINT",FACE,{"disambiguationData":[TD([[makeQuery(id+"F17.imprint","IMPRINT",EDGE,{"derivedFrom":sQuery(id+"F17.wireOp",EDGE,"E74.1.0")}),-1.0]])]});
            var Q1;
            Q1=sQuery(id+"F17.wireOp",EDGE,"E74.1.3");
            revolve(context, id + "F28", {"operationType" : NewBodyOperationType.REMOVE, "surfaceOperationType" : NewSurfaceOperationType.NEW, "entities" : qUnion([Q0]), "axis" : qUnion([Q1]), "revolveType" : RevolveType.FULL, "oppositeDirection" : true});
        }
        {
            var Q0;
            {var subQ0=sQuery(id+"F17.wireOp",EDGE,"E73");Q0=makeQuery(id+"F17.imprint","IMPRINT",FACE,{"disambiguationData":[TD([[makeQuery(id+"F17.imprint","IMPRINT",EDGE,{"derivedFrom":subQ0}),-1.0]])]});}
            var Q1;
            {var subQ0=sQuery(id+"F17.wireOp",EDGE,"E71");Q1=makeQuery(id+"F17.imprint","IMPRINT",FACE,{"disambiguationData":[TD([[makeQuery(id+"F17.imprint","IMPRINT",EDGE,{"derivedFrom":subQ0}),-1.0]])]});}
            var Q2;
            {var subQ0=sQuery(id+"F17.wireOp",EDGE,"E70");var subQ1=makeQuery(id+"F16.opExtrude","CAP_EDGE",EDGE,{"disambiguationData":[OSD([sQuery(id+"F15.wireOp",EDGE,"E34")])],"isStart":false});var subQ2=makeQuery(id+"F17.imprint","INTERSECT",VERTEX,{"derivedFrom":[subQ1,subQ0]});Q2=makeQuery(id+"F17.imprint","IMPRINT",FACE,{"disambiguationData":[TD([[makeQuery(id+"F17.imprint","IMPRINT",EDGE,{"disambiguationData":[TD([[subQ2,-1.0]])],"derivedFrom":subQ0}),-1.0]])]});}
            var Q3;
            Q3=sQuery(id+"F17.wireOp",EDGE,"E70");
            revolve(context, id + "F29", {"operationType" : NewBodyOperationType.REMOVE, "surfaceOperationType" : NewSurfaceOperationType.NEW, "entities" : qUnion([Q0, Q1, Q2]), "axis" : qUnion([Q3]), "revolveType" : RevolveType.FULL, "oppositeDirection" : true});
        }
    });
